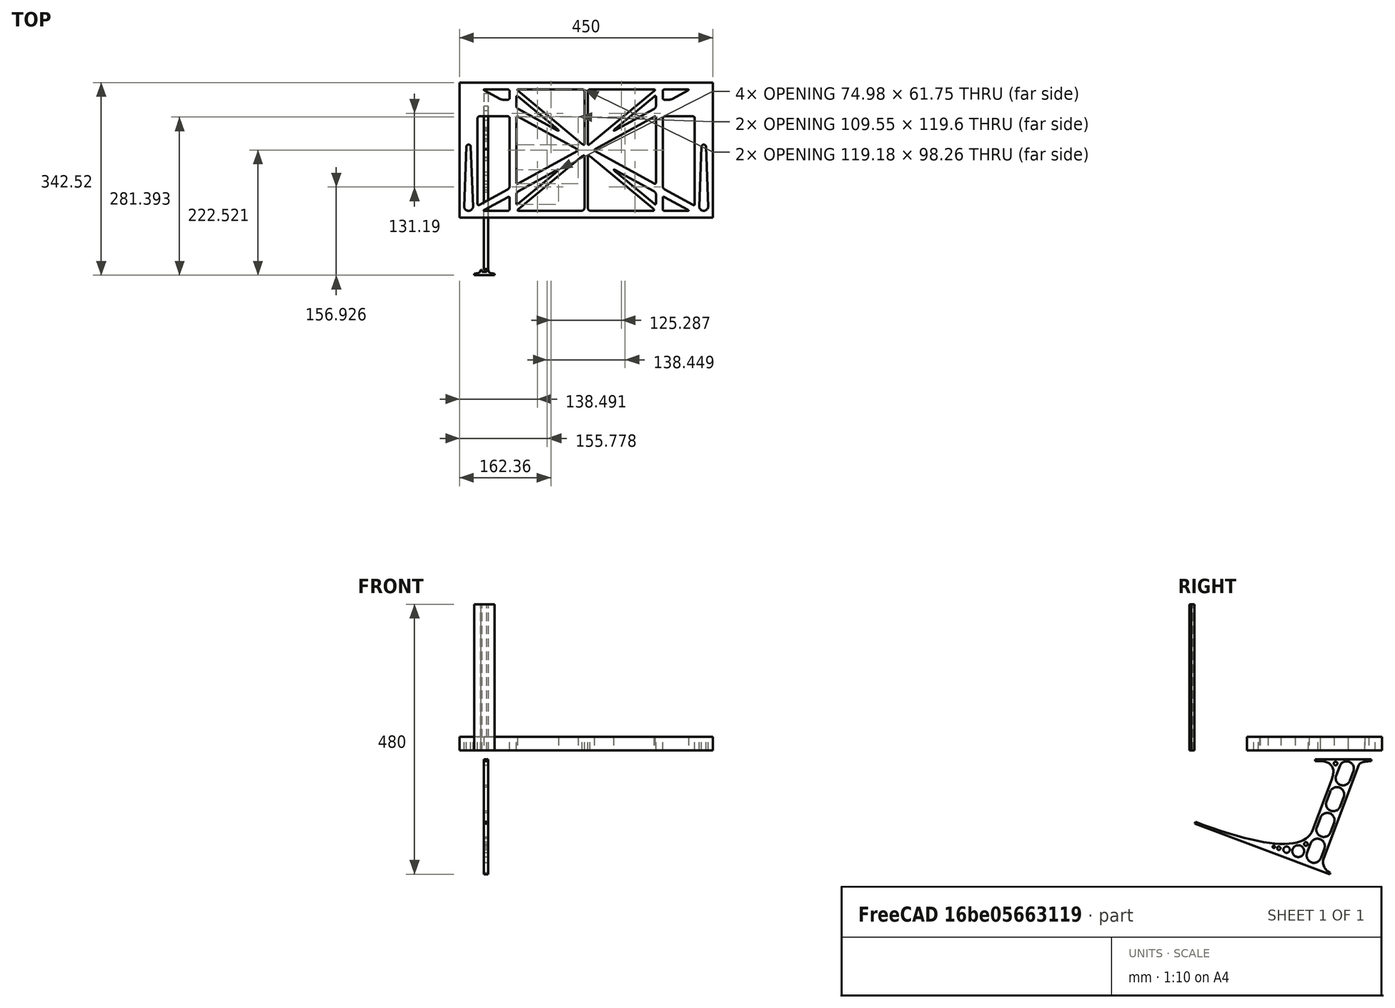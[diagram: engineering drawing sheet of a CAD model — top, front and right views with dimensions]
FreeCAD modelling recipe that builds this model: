
FCSTD DOCUMENT  (FreeCAD 0.19R0.19.2)
Label: laptopStand175FCStd
License: All rights reserved
LicenseURL: http://en.wikipedia.org/wiki/All_rights_reserved
objects: Sketcher::SketchObject×4, Part::Extrusion×3
note: 7 computed .brp shape members not serialized (recipe doc carries the construction recipe); baked Part::Feature solids carry a one-line shape summary decoded from their .brp

FEATURE [Sketcher::SketchObject] Sketch
  FullyConstrained = false
  sketch-geometry (349):
    g0: LineSegment StartX=-10.9272 StartY=-82.7794 StartZ=0 EndX=46.0728 EndY=-51.4823 EndZ=0
    g1: LineSegment StartX=-10.9272 StartY=76.4095 StartZ=0 EndX=-10.9272 EndY=-82.7794 EndZ=0
    g2: LineSegment StartX=46.0728 StartY=76.4095 StartZ=0 EndX=46.0728 EndY=-51.4823 EndZ=0
    g3: LineSegment StartX=-42.9272 StartY=136.221 StartZ=0 EndX=-42.9272 EndY=-103.779 EndZ=0
    g4: LineSegment StartX=407.073 StartY=136.221 StartZ=0 EndX=407.073 EndY=-103.779 EndZ=0
    g5: ArcOfCircle CenterX=-26.9272 CenterY=-83.7794 CenterZ=0 NormalX=0 NormalY=0 NormalZ=1 AngleXU=0 Radius=8 StartAngle=3.14159 EndAngle=6.28319
    g6: ArcOfCircle CenterX=391.073 CenterY=22.1087 CenterZ=0 NormalX=0 NormalY=0 NormalZ=1 AngleXU=0 Radius=8 StartAngle=-4.4e-15 EndAngle=3.14159
    g7: LineSegment StartX=399.073 StartY=22.1087 StartZ=0 EndX=399.073 EndY=-83.7794 EndZ=0
    g8: LineSegment StartX=383.073 StartY=22.1087 StartZ=0 EndX=383.073 EndY=-83.7794 EndZ=0
    g9: ArcOfCircle CenterX=391.073 CenterY=-83.7794 CenterZ=0 NormalX=0 NormalY=0 NormalZ=1 AngleXU=0 Radius=8 StartAngle=3.14159 EndAngle=6.28319
    g10: Circle CenterX=175.022 CenterY=27.0628 CenterZ=0 NormalX=0 NormalY=0 NormalZ=1 AngleXU=0 Radius=1
    g11: Circle CenterX=179.022 CenterY=24.8665 CenterZ=0 NormalX=0 NormalY=0 NormalZ=1 AngleXU=0 Radius=1
    g12: Circle CenterX=179.022 CenterY=27.0628 CenterZ=0 NormalX=0 NormalY=0 NormalZ=1 AngleXU=0 Radius=1
    g13: BSplineCurve PolesCount=3 KnotsCount=2 Degree=2 IsPeriodic=0
    g14: GeomPoint X=175.022 Y=27.0628 Z=0
    g15: GeomPoint X=179.022 Y=27.0628 Z=0
    g16: Circle CenterX=189.124 CenterY=27.0628 CenterZ=0 NormalX=0 NormalY=0 NormalZ=1 AngleXU=0 Radius=1
    g17: Circle CenterX=185.124 CenterY=24.8665 CenterZ=0 NormalX=0 NormalY=0 NormalZ=1 AngleXU=0 Radius=1
    g18: Circle CenterX=185.124 CenterY=27.0628 CenterZ=0 NormalX=0 NormalY=0 NormalZ=1 AngleXU=0 Radius=1
    g19: BSplineCurve PolesCount=3 KnotsCount=2 Degree=2 IsPeriodic=0
    g20: GeomPoint X=189.124 Y=27.0628 Z=0
    g21: GeomPoint X=185.124 Y=27.0628 Z=0
    g22: Circle CenterX=175.022 CenterY=5.37834 CenterZ=0 NormalX=0 NormalY=0 NormalZ=1 AngleXU=0 Radius=1
    g23: Circle CenterX=179.022 CenterY=7.57463 CenterZ=0 NormalX=0 NormalY=0 NormalZ=1 AngleXU=0 Radius=1
    g24: Circle CenterX=179.022 CenterY=5.34704 CenterZ=0 NormalX=0 NormalY=0 NormalZ=1 AngleXU=0 Radius=1
    g25: BSplineCurve PolesCount=3 KnotsCount=2 Degree=2 IsPeriodic=0
    g26: GeomPoint X=175.022 Y=5.37834 Z=0
    g27: GeomPoint X=179.022 Y=5.34704 Z=0
    g28: Circle CenterX=189.124 CenterY=5.37834 CenterZ=0 NormalX=0 NormalY=0 NormalZ=1 AngleXU=0 Radius=1
    g29: Circle CenterX=185.124 CenterY=7.57463 CenterZ=0 NormalX=0 NormalY=0 NormalZ=1 AngleXU=0 Radius=1
    g30: Circle CenterX=185.124 CenterY=5.34704 CenterZ=0 NormalX=0 NormalY=0 NormalZ=1 AngleXU=0 Radius=1
    g31: BSplineCurve PolesCount=3 KnotsCount=2 Degree=2 IsPeriodic=0
    g32: GeomPoint X=189.124 Y=5.37834 Z=0
    g33: GeomPoint X=185.124 Y=5.34704 Z=0
    g34: Circle CenterX=165.871 CenterY=18.1458 CenterZ=0 NormalX=0 NormalY=0 NormalZ=1 AngleXU=0 Radius=1
    g35: Circle CenterX=169.377 CenterY=16.2206 CenterZ=0 NormalX=0 NormalY=0 NormalZ=1 AngleXU=0 Radius=1
    g36: Circle CenterX=165.871 CenterY=14.2954 CenterZ=0 NormalX=0 NormalY=0 NormalZ=1 AngleXU=0 Radius=1
    g37: BSplineCurve PolesCount=3 KnotsCount=2 Degree=2 IsPeriodic=0
    g38: GeomPoint X=165.871 Y=18.1458 Z=0
    g39: GeomPoint X=165.871 Y=14.2954 Z=0
    g40: Circle CenterX=198.275 CenterY=18.1458 CenterZ=0 NormalX=0 NormalY=0 NormalZ=1 AngleXU=0 Radius=1
    g41: Circle CenterX=194.768 CenterY=16.2206 CenterZ=0 NormalX=0 NormalY=0 NormalZ=1 AngleXU=0 Radius=1
    g42: Circle CenterX=198.275 CenterY=14.2954 CenterZ=0 NormalX=0 NormalY=0 NormalZ=1 AngleXU=0 Radius=1
    g43: BSplineCurve PolesCount=3 KnotsCount=2 Degree=2 IsPeriodic=0
    g44: GeomPoint X=198.275 Y=18.1458 Z=0
    g45: GeomPoint X=198.275 Y=14.2954 Z=0
    g46: LineSegment StartX=407.073 StartY=-103.779 StartZ=0 EndX=-42.9272 EndY=-103.779 EndZ=0
    g47: LineSegment StartX=407.073 StartY=136.221 StartZ=0 EndX=-42.9272 EndY=136.221 EndZ=0
    g48: LineSegment StartX=46.0728 StartY=76.4095 StartZ=0 EndX=-10.9272 EndY=76.4095 EndZ=0
    g49: Circle CenterX=125.607 CenterY=54.1951 CenterZ=0 NormalX=0 NormalY=0 NormalZ=1 AngleXU=0 Radius=1
    g50: Circle CenterX=139.632 CenterY=46.4944 CenterZ=0 NormalX=0 NormalY=0 NormalZ=1 AngleXU=0 Radius=1
    g51: Circle CenterX=127.326 CenterY=56.7187 CenterZ=0 NormalX=0 NormalY=0 NormalZ=1 AngleXU=0 Radius=1
    g52: BSplineCurve PolesCount=3 KnotsCount=2 Degree=2 IsPeriodic=0
    g53: GeomPoint X=125.607 Y=54.1951 Z=0
    g54: GeomPoint X=127.326 Y=56.7187 Z=0
    g55: Circle CenterX=236.821 CenterY=56.7187 CenterZ=0 NormalX=0 NormalY=0 NormalZ=1 AngleXU=0 Radius=1
    g56: Circle CenterX=224.513 CenterY=46.4944 CenterZ=0 NormalX=0 NormalY=0 NormalZ=1 AngleXU=0 Radius=1
    g57: Circle CenterX=238.538 CenterY=54.1951 CenterZ=0 NormalX=0 NormalY=0 NormalZ=1 AngleXU=0 Radius=1
    g58: BSplineCurve PolesCount=3 KnotsCount=2 Degree=2 IsPeriodic=0
    g59: GeomPoint X=236.821 Y=56.7187 Z=0
    g60: GeomPoint X=238.538 Y=54.1951 Z=0
    g61: Circle CenterX=238.538 CenterY=-21.7539 CenterZ=0 NormalX=0 NormalY=0 NormalZ=1 AngleXU=0 Radius=1
    g62: Circle CenterX=224.513 CenterY=-14.0532 CenterZ=0 NormalX=0 NormalY=0 NormalZ=1 AngleXU=0 Radius=1
    g63: Circle CenterX=236.821 CenterY=-24.2775 CenterZ=0 NormalX=0 NormalY=0 NormalZ=1 AngleXU=0 Radius=1
    g64: BSplineCurve PolesCount=3 KnotsCount=2 Degree=2 IsPeriodic=0
    g65: GeomPoint X=238.538 Y=-21.7539 Z=0
    g66: GeomPoint X=236.821 Y=-24.2775 Z=0
    g67: Circle CenterX=125.607 CenterY=-21.7539 CenterZ=0 NormalX=0 NormalY=0 NormalZ=1 AngleXU=0 Radius=1
    g68: Circle CenterX=139.632 CenterY=-14.0532 CenterZ=0 NormalX=0 NormalY=0 NormalZ=1 AngleXU=0 Radius=1
    g69: Circle CenterX=127.325 CenterY=-24.2775 CenterZ=0 NormalX=0 NormalY=0 NormalZ=1 AngleXU=0 Radius=1
    g70: BSplineCurve PolesCount=3 KnotsCount=2 Degree=2 IsPeriodic=0
    g71: GeomPoint X=125.607 Y=-21.7539 Z=0
    g72: GeomPoint X=127.325 Y=-24.2775 Z=0
    g73: Circle CenterX=302.996 CenterY=111.695 CenterZ=0 NormalX=0 NormalY=0 NormalZ=1 AngleXU=0 Radius=1
    g74: Circle CenterX=306.073 CenterY=114.251 CenterZ=0 NormalX=0 NormalY=0 NormalZ=1 AngleXU=0 Radius=1
    g75: Circle CenterX=306.073 CenterY=110.251 CenterZ=0 NormalX=0 NormalY=0 NormalZ=1 AngleXU=0 Radius=1
    g76: BSplineCurve PolesCount=3 KnotsCount=2 Degree=2 IsPeriodic=0
    g77: GeomPoint X=302.996 Y=111.695 Z=0
    g78: GeomPoint X=306.073 Y=110.251 Z=0
    g79: Circle CenterX=306.073 CenterY=95.2763 CenterZ=0 NormalX=0 NormalY=0 NormalZ=1 AngleXU=0 Radius=1
    g80: Circle CenterX=306.073 CenterY=91.2763 CenterZ=0 NormalX=0 NormalY=0 NormalZ=1 AngleXU=0 Radius=1
    g81: Circle CenterX=302.567 CenterY=89.3511 CenterZ=0 NormalX=0 NormalY=0 NormalZ=1 AngleXU=0 Radius=1
    g82: BSplineCurve PolesCount=3 KnotsCount=2 Degree=2 IsPeriodic=0
    g83: GeomPoint X=306.073 Y=95.2763 Z=0
    g84: GeomPoint X=302.567 Y=89.3511 Z=0
    g85: LineSegment StartX=306.073 StartY=110.251 StartZ=0 EndX=306.073 EndY=95.2763 EndZ=0
    g86: LineSegment StartX=302.996 StartY=111.695 StartZ=0 EndX=236.821 EndY=56.7187 EndZ=0
    g87: LineSegment StartX=238.538 StartY=54.1951 StartZ=0 EndX=302.567 EndY=89.3511 EndZ=0
    g88: Circle CenterX=61.1496 CenterY=111.695 CenterZ=0 NormalX=0 NormalY=0 NormalZ=1 AngleXU=0 Radius=1
    g89: Circle CenterX=58.0728 CenterY=114.251 CenterZ=0 NormalX=0 NormalY=0 NormalZ=1 AngleXU=0 Radius=1
    g90: Circle CenterX=58.0728 CenterY=110.251 CenterZ=0 NormalX=0 NormalY=0 NormalZ=1 AngleXU=0 Radius=1
    g91: BSplineCurve PolesCount=3 KnotsCount=2 Degree=2 IsPeriodic=0
    g92: GeomPoint X=61.1496 Y=111.695 Z=0
    g93: GeomPoint X=58.0728 Y=110.251 Z=0
    g94: Circle CenterX=61.5791 CenterY=89.3511 CenterZ=0 NormalX=0 NormalY=0 NormalZ=1 AngleXU=0 Radius=1
    g95: Circle CenterX=58.0728 CenterY=91.2763 CenterZ=0 NormalX=0 NormalY=0 NormalZ=1 AngleXU=0 Radius=1
    g96: Circle CenterX=58.0728 CenterY=95.2763 CenterZ=0 NormalX=0 NormalY=0 NormalZ=1 AngleXU=0 Radius=1
    g97: BSplineCurve PolesCount=3 KnotsCount=2 Degree=2 IsPeriodic=0
    g98: GeomPoint X=61.5791 Y=89.3511 Z=0
    g99: GeomPoint X=58.0728 Y=95.2763 Z=0
    g100: LineSegment StartX=58.0728 StartY=110.251 StartZ=0 EndX=58.0728 EndY=95.2763 EndZ=0
    g101: LineSegment StartX=61.1496 StartY=111.695 StartZ=0 EndX=127.326 EndY=56.7187 EndZ=0
    g102: LineSegment StartX=125.607 StartY=54.1951 StartZ=0 EndX=61.5791 EndY=89.3511 EndZ=0
    g103: Circle CenterX=61.5791 CenterY=-56.9099 CenterZ=0 NormalX=0 NormalY=0 NormalZ=1 AngleXU=0 Radius=1
    g104: Circle CenterX=58.0728 CenterY=-58.8351 CenterZ=0 NormalX=0 NormalY=0 NormalZ=1 AngleXU=0 Radius=1
    g105: Circle CenterX=58.0728 CenterY=-62.8351 CenterZ=0 NormalX=0 NormalY=0 NormalZ=1 AngleXU=0 Radius=1
    g106: BSplineCurve PolesCount=3 KnotsCount=2 Degree=2 IsPeriodic=0
    g107: GeomPoint X=61.5791 Y=-56.9099 Z=0
    g108: GeomPoint X=58.0728 Y=-62.8351 Z=0
    g109: Circle CenterX=58.0728 CenterY=-77.8102 CenterZ=0 NormalX=0 NormalY=0 NormalZ=1 AngleXU=0 Radius=1
    g110: Circle CenterX=58.0728 CenterY=-81.8102 CenterZ=0 NormalX=0 NormalY=0 NormalZ=1 AngleXU=0 Radius=1
    g111: Circle CenterX=61.1496 CenterY=-79.2541 CenterZ=0 NormalX=0 NormalY=0 NormalZ=1 AngleXU=0 Radius=1
    g112: BSplineCurve PolesCount=3 KnotsCount=2 Degree=2 IsPeriodic=0
    g113: GeomPoint X=58.0728 Y=-77.8102 Z=0
    g114: GeomPoint X=61.1496 Y=-79.2541 Z=0
    g115: LineSegment StartX=58.0728 StartY=-62.8351 StartZ=0 EndX=58.0728 EndY=-77.8102 EndZ=0
    g116: LineSegment StartX=61.1496 StartY=-79.2541 StartZ=0 EndX=127.325 EndY=-24.2775 EndZ=0
    g117: LineSegment StartX=125.607 StartY=-21.7539 StartZ=0 EndX=61.5791 EndY=-56.9099 EndZ=0
    g118: Circle CenterX=302.567 CenterY=-56.9099 CenterZ=0 NormalX=0 NormalY=0 NormalZ=1 AngleXU=0 Radius=1
    g119: Circle CenterX=306.073 CenterY=-58.8351 CenterZ=0 NormalX=0 NormalY=0 NormalZ=1 AngleXU=0 Radius=1
    g120: Circle CenterX=306.073 CenterY=-62.8351 CenterZ=0 NormalX=0 NormalY=0 NormalZ=1 AngleXU=0 Radius=1
    g121: BSplineCurve PolesCount=3 KnotsCount=2 Degree=2 IsPeriodic=0
    g122: GeomPoint X=302.567 Y=-56.9099 Z=0
    g123: GeomPoint X=306.073 Y=-62.8351 Z=0
    g124: Circle CenterX=302.996 CenterY=-79.2541 CenterZ=0 NormalX=0 NormalY=0 NormalZ=1 AngleXU=0 Radius=1
    g125: Circle CenterX=306.073 CenterY=-81.8102 CenterZ=0 NormalX=0 NormalY=0 NormalZ=1 AngleXU=0 Radius=1
    g126: Circle CenterX=306.073 CenterY=-77.8102 CenterZ=0 NormalX=0 NormalY=0 NormalZ=1 AngleXU=0 Radius=1
    g127: BSplineCurve PolesCount=3 KnotsCount=2 Degree=2 IsPeriodic=0
    g128: GeomPoint X=302.996 Y=-79.2541 Z=0
    g129: GeomPoint X=306.073 Y=-77.8102 Z=0
    g130: LineSegment StartX=306.073 StartY=-62.8351 StartZ=0 EndX=306.073 EndY=-77.8102 EndZ=0
    g131: LineSegment StartX=302.996 StartY=-79.2541 StartZ=0 EndX=236.821 EndY=-24.2775 EndZ=0
    g132: LineSegment StartX=238.538 StartY=-21.7539 StartZ=0 EndX=302.567 EndY=-56.9099 EndZ=0
    g133: Circle CenterX=61.6457 CenterY=-88.8112 CenterZ=0 NormalX=0 NormalY=0 NormalZ=1 AngleXU=0 Radius=1
    g134: Circle CenterX=58.0728 CenterY=-91.7794 CenterZ=0 NormalX=0 NormalY=0 NormalZ=1 AngleXU=0 Radius=1
    g135: Circle CenterX=63.9135 CenterY=-91.7794 CenterZ=0 NormalX=0 NormalY=0 NormalZ=1 AngleXU=0 Radius=1
    g136: BSplineCurve PolesCount=3 KnotsCount=2 Degree=2 IsPeriodic=0
    g137: GeomPoint X=61.6457 Y=-88.8112 Z=0
    g138: GeomPoint X=63.9135 Y=-91.7794 Z=0
    g139: Circle CenterX=179.022 CenterY=-85.8163 CenterZ=0 NormalX=0 NormalY=0 NormalZ=1 AngleXU=0 Radius=1
    g140: Circle CenterX=179.022 CenterY=-91.7794 CenterZ=0 NormalX=0 NormalY=0 NormalZ=1 AngleXU=0 Radius=1
    g141: Circle CenterX=171.895 CenterY=-91.7794 CenterZ=0 NormalX=0 NormalY=0 NormalZ=1 AngleXU=0 Radius=1
    g142: BSplineCurve PolesCount=3 KnotsCount=2 Degree=2 IsPeriodic=0
    g143: GeomPoint X=179.022 Y=-85.8163 Z=0
    g144: GeomPoint X=171.895 Y=-91.7794 Z=0
    g145: Circle CenterX=185.124 CenterY=-86.2028 CenterZ=0 NormalX=0 NormalY=0 NormalZ=1 AngleXU=0 Radius=1
    g146: Circle CenterX=185.124 CenterY=-91.7794 CenterZ=0 NormalX=0 NormalY=0 NormalZ=1 AngleXU=0 Radius=1
    g147: Circle CenterX=191.747 CenterY=-91.7794 CenterZ=0 NormalX=0 NormalY=0 NormalZ=1 AngleXU=0 Radius=1
    g148: BSplineCurve PolesCount=3 KnotsCount=2 Degree=2 IsPeriodic=0
    g149: GeomPoint X=185.124 Y=-86.2028 Z=0
    g150: GeomPoint X=191.747 Y=-91.7794 Z=0
    g151: Circle CenterX=299.888 CenterY=-86.6413 CenterZ=0 NormalX=0 NormalY=0 NormalZ=1 AngleXU=0 Radius=1
    g152: Circle CenterX=306.073 CenterY=-91.7794 CenterZ=0 NormalX=0 NormalY=0 NormalZ=1 AngleXU=0 Radius=1
    g153: Circle CenterX=298.776 CenterY=-91.7794 CenterZ=0 NormalX=0 NormalY=0 NormalZ=1 AngleXU=0 Radius=1
    g154: BSplineCurve PolesCount=3 KnotsCount=2 Degree=2 IsPeriodic=0
    g155: GeomPoint X=299.888 Y=-86.6413 Z=0
    g156: GeomPoint X=298.776 Y=-91.7794 Z=0
    g157: LineSegment StartX=189.124 StartY=5.37834 StartZ=0 EndX=299.888 EndY=-86.6413 EndZ=0
    g158: LineSegment StartX=298.776 StartY=-91.7794 StartZ=0 EndX=191.747 EndY=-91.7794 EndZ=0
    g159: LineSegment StartX=185.124 StartY=-86.2028 StartZ=0 EndX=185.124 EndY=5.34704 EndZ=0
    g160: LineSegment StartX=179.022 StartY=5.34704 StartZ=0 EndX=179.022 EndY=-85.8163 EndZ=0
    g161: LineSegment StartX=171.895 StartY=-91.7794 StartZ=0 EndX=63.9135 EndY=-91.7794 EndZ=0
    g162: LineSegment StartX=61.6457 StartY=-88.8112 StartZ=0 EndX=175.022 EndY=5.37834 EndZ=0
    g163: Circle CenterX=302.073 CenterY=124.221 CenterZ=0 NormalX=0 NormalY=0 NormalZ=1 AngleXU=0 Radius=1
    g164: Circle CenterX=306.073 CenterY=124.221 CenterZ=0 NormalX=0 NormalY=0 NormalZ=1 AngleXU=0 Radius=1
    g165: Circle CenterX=302.996 CenterY=121.665 CenterZ=0 NormalX=0 NormalY=0 NormalZ=1 AngleXU=0 Radius=1
    g166: BSplineCurve PolesCount=3 KnotsCount=2 Degree=2 IsPeriodic=0
    g167: GeomPoint X=302.073 Y=124.221 Z=0
    g168: GeomPoint X=302.996 Y=121.665 Z=0
    g169: Circle CenterX=189.124 CenterY=124.221 CenterZ=0 NormalX=0 NormalY=0 NormalZ=1 AngleXU=0 Radius=1
    g170: Circle CenterX=185.124 CenterY=124.221 CenterZ=0 NormalX=0 NormalY=0 NormalZ=1 AngleXU=0 Radius=1
    g171: Circle CenterX=185.124 CenterY=120.221 CenterZ=0 NormalX=0 NormalY=0 NormalZ=1 AngleXU=0 Radius=1
    g172: BSplineCurve PolesCount=3 KnotsCount=2 Degree=2 IsPeriodic=0
    g173: GeomPoint X=189.124 Y=124.221 Z=0
    g174: GeomPoint X=185.124 Y=120.221 Z=0
    g175: Circle CenterX=175.022 CenterY=124.221 CenterZ=0 NormalX=0 NormalY=0 NormalZ=1 AngleXU=0 Radius=1
    g176: Circle CenterX=179.022 CenterY=124.221 CenterZ=0 NormalX=0 NormalY=0 NormalZ=1 AngleXU=0 Radius=1
    g177: Circle CenterX=179.022 CenterY=120.221 CenterZ=0 NormalX=0 NormalY=0 NormalZ=1 AngleXU=0 Radius=1
    g178: BSplineCurve PolesCount=3 KnotsCount=2 Degree=2 IsPeriodic=0
    g179: GeomPoint X=175.022 Y=124.221 Z=0
    g180: GeomPoint X=179.022 Y=120.221 Z=0
    g181: Circle CenterX=62.0728 CenterY=124.221 CenterZ=0 NormalX=0 NormalY=0 NormalZ=1 AngleXU=0 Radius=1
    g182: Circle CenterX=58.0728 CenterY=124.221 CenterZ=0 NormalX=0 NormalY=0 NormalZ=1 AngleXU=0 Radius=1
    g183: Circle CenterX=61.1496 CenterY=121.665 CenterZ=0 NormalX=0 NormalY=0 NormalZ=1 AngleXU=0 Radius=1
    g184: BSplineCurve PolesCount=3 KnotsCount=2 Degree=2 IsPeriodic=0
    g185: GeomPoint X=62.0728 Y=124.221 Z=0
    g186: GeomPoint X=61.1496 Y=121.665 Z=0
    g187: LineSegment StartX=62.0728 StartY=124.221 StartZ=0 EndX=175.022 EndY=124.221 EndZ=0
    g188: LineSegment StartX=179.022 StartY=120.221 StartZ=0 EndX=179.022 EndY=27.0628 EndZ=0
    g189: LineSegment StartX=185.124 StartY=27.0628 StartZ=0 EndX=185.124 EndY=120.221 EndZ=0
    g190: LineSegment StartX=189.124 StartY=124.221 StartZ=0 EndX=302.073 EndY=124.221 EndZ=0
    g191: LineSegment StartX=302.996 StartY=121.665 StartZ=0 EndX=189.124 EndY=27.0628 EndZ=0
    g192: LineSegment StartX=175.022 StartY=27.0628 StartZ=0 EndX=61.1496 EndY=121.665 EndZ=0
    g193: Circle CenterX=61.5791 CenterY=75.4095 CenterZ=0 NormalX=0 NormalY=0 NormalZ=1 AngleXU=0 Radius=1
    g194: Circle CenterX=58.0728 CenterY=77.3346 CenterZ=0 NormalX=0 NormalY=0 NormalZ=1 AngleXU=0 Radius=1
    g195: Circle CenterX=58.0728 CenterY=73.3346 CenterZ=0 NormalX=0 NormalY=0 NormalZ=1 AngleXU=0 Radius=1
    g196: BSplineCurve PolesCount=3 KnotsCount=2 Degree=2 IsPeriodic=0
    g197: GeomPoint X=61.5791 Y=75.4095 Z=0
    g198: GeomPoint X=58.0728 Y=73.3346 Z=0
    g199: Circle CenterX=58.0728 CenterY=-40.8935 CenterZ=0 NormalX=0 NormalY=0 NormalZ=1 AngleXU=0 Radius=1
    g200: Circle CenterX=58.0728 CenterY=-44.8935 CenterZ=0 NormalX=0 NormalY=0 NormalZ=1 AngleXU=0 Radius=1
    g201: Circle CenterX=61.5791 CenterY=-42.9683 CenterZ=0 NormalX=0 NormalY=0 NormalZ=1 AngleXU=0 Radius=1
    g202: BSplineCurve PolesCount=3 KnotsCount=2 Degree=2 IsPeriodic=0
    g203: GeomPoint X=58.0728 Y=-40.8935 Z=0
    g204: GeomPoint X=61.5791 Y=-42.9683 Z=0
    g205: LineSegment StartX=61.5791 StartY=-42.9683 StartZ=0 EndX=165.871 EndY=14.2954 EndZ=0
    g206: LineSegment StartX=165.871 StartY=18.1458 StartZ=0 EndX=61.5791 EndY=75.4095 EndZ=0
    g207: LineSegment StartX=58.0728 StartY=73.3346 StartZ=0 EndX=58.0728 EndY=-40.8935 EndZ=0
    g208: Circle CenterX=302.567 CenterY=-42.9683 CenterZ=0 NormalX=0 NormalY=0 NormalZ=1 AngleXU=0 Radius=1
    g209: Circle CenterX=306.073 CenterY=-44.8935 CenterZ=0 NormalX=0 NormalY=0 NormalZ=1 AngleXU=0 Radius=1
    g210: Circle CenterX=306.073 CenterY=-40.8935 CenterZ=0 NormalX=0 NormalY=0 NormalZ=1 AngleXU=0 Radius=1
    g211: BSplineCurve PolesCount=3 KnotsCount=2 Degree=2 IsPeriodic=0
    g212: GeomPoint X=302.567 Y=-42.9683 Z=0
    g213: GeomPoint X=306.073 Y=-40.8935 Z=0
    g214: Circle CenterX=306.073 CenterY=73.3346 CenterZ=0 NormalX=0 NormalY=0 NormalZ=1 AngleXU=0 Radius=1
    g215: Circle CenterX=306.073 CenterY=77.3346 CenterZ=0 NormalX=0 NormalY=0 NormalZ=1 AngleXU=0 Radius=1
    g216: Circle CenterX=302.567 CenterY=75.4095 CenterZ=0 NormalX=0 NormalY=0 NormalZ=1 AngleXU=0 Radius=1
    g217: BSplineCurve PolesCount=3 KnotsCount=2 Degree=2 IsPeriodic=0
    g218: GeomPoint X=306.073 Y=73.3346 Z=0
    g219: GeomPoint X=302.567 Y=75.4095 Z=0
    g220: LineSegment StartX=302.567 StartY=-42.9683 StartZ=0 EndX=198.275 EndY=14.2954 EndZ=0
    g221: LineSegment StartX=198.275 StartY=18.1458 StartZ=0 EndX=302.567 EndY=75.4095 EndZ=0
    g222: LineSegment StartX=306.073 StartY=73.3346 StartZ=0 EndX=306.073 EndY=-40.8935 EndZ=0
    g223: LineSegment StartX=322.073 StartY=105.865 StartZ=0 EndX=328.643 EndY=105.865 EndZ=0
    g224: LineSegment StartX=318.073 StartY=120.221 StartZ=0 EndX=318.073 EndY=109.865 EndZ=0
    g225: LineSegment StartX=336.157 StartY=107.779 StartZ=0 EndX=362.567 EndY=122.294 EndZ=0
    g226: Circle CenterX=362.073 CenterY=124.221 CenterZ=0 NormalX=0 NormalY=0 NormalZ=1 AngleXU=0 Radius=1
    g227: Circle CenterX=366.073 CenterY=124.221 CenterZ=0 NormalX=0 NormalY=0 NormalZ=1 AngleXU=0 Radius=1
    g228: Circle CenterX=362.567 CenterY=122.294 CenterZ=0 NormalX=0 NormalY=0 NormalZ=1 AngleXU=0 Radius=1
    g229: BSplineCurve PolesCount=3 KnotsCount=2 Degree=2 IsPeriodic=0
    g230: GeomPoint X=362.073 Y=124.221 Z=0
    g231: GeomPoint X=362.567 Y=122.294 Z=0
    g232: Circle CenterX=322.073 CenterY=124.221 CenterZ=0 NormalX=0 NormalY=0 NormalZ=1 AngleXU=0 Radius=1
    g233: Circle CenterX=318.073 CenterY=124.221 CenterZ=0 NormalX=0 NormalY=0 NormalZ=1 AngleXU=0 Radius=1
    g234: Circle CenterX=318.073 CenterY=120.221 CenterZ=0 NormalX=0 NormalY=0 NormalZ=1 AngleXU=0 Radius=1
    g235: BSplineCurve PolesCount=3 KnotsCount=2 Degree=2 IsPeriodic=0
    g236: GeomPoint X=322.073 Y=124.221 Z=0
    g237: GeomPoint X=318.073 Y=120.221 Z=0
    g238: Circle CenterX=322.073 CenterY=105.865 CenterZ=0 NormalX=0 NormalY=0 NormalZ=1 AngleXU=0 Radius=1
    g239: Circle CenterX=318.073 CenterY=105.865 CenterZ=0 NormalX=0 NormalY=0 NormalZ=1 AngleXU=0 Radius=1
    g240: Circle CenterX=318.073 CenterY=109.865 CenterZ=0 NormalX=0 NormalY=0 NormalZ=1 AngleXU=0 Radius=1
    g241: BSplineCurve PolesCount=3 KnotsCount=2 Degree=2 IsPeriodic=0
    g242: GeomPoint X=322.073 Y=105.865 Z=0
    g243: GeomPoint X=318.073 Y=109.865 Z=0
    g244: Circle CenterX=336.157 CenterY=107.779 CenterZ=0 NormalX=0 NormalY=0 NormalZ=1 AngleXU=0 Radius=1
    g245: Circle CenterX=332.651 CenterY=105.853 CenterZ=0 NormalX=0 NormalY=0 NormalZ=1 AngleXU=0 Radius=1
    g246: Circle CenterX=328.643 CenterY=105.865 CenterZ=0 NormalX=0 NormalY=0 NormalZ=1 AngleXU=0 Radius=1
    g247: BSplineCurve PolesCount=3 KnotsCount=2 Degree=2 IsPeriodic=0
    g248: GeomPoint X=336.157 Y=107.779 Z=0
    g249: GeomPoint X=328.643 Y=105.865 Z=0
    g250: LineSegment StartX=322.073 StartY=124.221 StartZ=0 EndX=362.073 EndY=124.221 EndZ=0
    g251: Circle CenterX=371.567 CenterY=-80.8644 CenterZ=0 NormalX=0 NormalY=0 NormalZ=1 AngleXU=0 Radius=1
    g252: Circle CenterX=375.073 CenterY=-82.7896 CenterZ=0 NormalX=0 NormalY=0 NormalZ=1 AngleXU=0 Radius=1
    g253: Circle CenterX=375.073 CenterY=-78.7896 CenterZ=0 NormalX=0 NormalY=0 NormalZ=1 AngleXU=0 Radius=1
    g254: BSplineCurve PolesCount=3 KnotsCount=2 Degree=2 IsPeriodic=0
    g255: GeomPoint X=371.567 Y=-80.8644 Z=0
    g256: GeomPoint X=375.073 Y=-78.7896 Z=0
    g257: Circle CenterX=321.579 CenterY=-53.4075 CenterZ=0 NormalX=0 NormalY=0 NormalZ=1 AngleXU=0 Radius=1
    g258: Circle CenterX=318.073 CenterY=-51.4823 CenterZ=0 NormalX=0 NormalY=0 NormalZ=1 AngleXU=0 Radius=1
    g259: Circle CenterX=318.073 CenterY=-47.4805 CenterZ=0 NormalX=0 NormalY=0 NormalZ=1 AngleXU=0 Radius=1
    g260: BSplineCurve PolesCount=3 KnotsCount=2 Degree=2 IsPeriodic=0
    g261: GeomPoint X=321.579 Y=-53.4075 Z=0
    g262: GeomPoint X=318.073 Y=-47.4805 Z=0
    g263: LineSegment StartX=371.567 StartY=-80.8644 StartZ=0 EndX=321.579 EndY=-53.4075 EndZ=0
    g264: Circle CenterX=321.579 CenterY=-67.3492 CenterZ=0 NormalX=0 NormalY=0 NormalZ=1 AngleXU=0 Radius=1
    g265: Circle CenterX=318.073 CenterY=-65.424 CenterZ=0 NormalX=0 NormalY=0 NormalZ=1 AngleXU=0 Radius=1
    g266: Circle CenterX=318.073 CenterY=-69.424 CenterZ=0 NormalX=0 NormalY=0 NormalZ=1 AngleXU=0 Radius=1
    g267: BSplineCurve PolesCount=3 KnotsCount=2 Degree=2 IsPeriodic=0
    g268: GeomPoint X=321.579 Y=-67.3492 Z=0
    g269: GeomPoint X=318.073 Y=-69.424 Z=0
    g270: Circle CenterX=362.567 CenterY=-89.8542 CenterZ=0 NormalX=0 NormalY=0 NormalZ=1 AngleXU=0 Radius=1
    g271: Circle CenterX=366.073 CenterY=-91.7794 CenterZ=0 NormalX=0 NormalY=0 NormalZ=1 AngleXU=0 Radius=1
    g272: Circle CenterX=362.073 CenterY=-91.7794 CenterZ=0 NormalX=0 NormalY=0 NormalZ=1 AngleXU=0 Radius=1
    g273: BSplineCurve PolesCount=3 KnotsCount=2 Degree=2 IsPeriodic=0
    g274: GeomPoint X=362.567 Y=-89.8542 Z=0
    g275: GeomPoint X=362.073 Y=-91.7794 Z=0
    g276: Circle CenterX=322.073 CenterY=-91.7794 CenterZ=0 NormalX=0 NormalY=0 NormalZ=1 AngleXU=0 Radius=1
    g277: Circle CenterX=318.073 CenterY=-91.7794 CenterZ=0 NormalX=0 NormalY=0 NormalZ=1 AngleXU=0 Radius=1
    g278: Circle CenterX=318.073 CenterY=-87.7794 CenterZ=0 NormalX=0 NormalY=0 NormalZ=1 AngleXU=0 Radius=1
    g279: BSplineCurve PolesCount=3 KnotsCount=2 Degree=2 IsPeriodic=0
    g280: GeomPoint X=322.073 Y=-91.7794 Z=0
    g281: GeomPoint X=318.073 Y=-87.7794 Z=0
    g282: LineSegment StartX=362.567 StartY=-89.8542 StartZ=0 EndX=321.579 EndY=-67.3492 EndZ=0
    g283: LineSegment StartX=318.073 StartY=-69.424 StartZ=0 EndX=318.073 EndY=-87.7794 EndZ=0
    g284: LineSegment StartX=322.073 StartY=-91.7794 StartZ=0 EndX=362.073 EndY=-91.7794 EndZ=0
    g285: Circle CenterX=2.07281 CenterY=124.221 CenterZ=0 NormalX=0 NormalY=0 NormalZ=1 AngleXU=0 Radius=1
    g286: Circle CenterX=1.57905 CenterY=122.295 CenterZ=0 NormalX=0 NormalY=0 NormalZ=1 AngleXU=0 Radius=1
    g287: BSplineCurve PolesCount=3 KnotsCount=2 Degree=2 IsPeriodic=0
    g288: GeomPoint X=2.07281 Y=124.221 Z=0
    g289: GeomPoint X=1.57905 Y=122.295 Z=0
    g290: Circle CenterX=42.0728 CenterY=124.221 CenterZ=0 NormalX=0 NormalY=0 NormalZ=1 AngleXU=0 Radius=1
    g291: Circle CenterX=46.0728 CenterY=124.221 CenterZ=0 NormalX=0 NormalY=0 NormalZ=1 AngleXU=0 Radius=1
    g292: Circle CenterX=46.0728 CenterY=120.221 CenterZ=0 NormalX=0 NormalY=0 NormalZ=1 AngleXU=0 Radius=1
    g293: BSplineCurve PolesCount=3 KnotsCount=2 Degree=2 IsPeriodic=0
    g294: GeomPoint X=42.0728 Y=124.221 Z=0
    g295: GeomPoint X=46.0728 Y=120.221 Z=0
    g296: Circle CenterX=46.0728 CenterY=109.865 CenterZ=0 NormalX=0 NormalY=0 NormalZ=1 AngleXU=0 Radius=1
    g297: Circle CenterX=46.0728 CenterY=105.865 CenterZ=0 NormalX=0 NormalY=0 NormalZ=1 AngleXU=0 Radius=1
    g298: Circle CenterX=42.0728 CenterY=105.865 CenterZ=0 NormalX=0 NormalY=0 NormalZ=1 AngleXU=0 Radius=1
    g299: BSplineCurve PolesCount=3 KnotsCount=2 Degree=2 IsPeriodic=0
    g300: GeomPoint X=46.0728 Y=109.865 Z=0
    g301: GeomPoint X=42.0728 Y=105.865 Z=0
    g302: Circle CenterX=35.5028 CenterY=105.865 CenterZ=0 NormalX=0 NormalY=0 NormalZ=1 AngleXU=0 Radius=1
    g303: Circle CenterX=31.5028 CenterY=105.865 CenterZ=0 NormalX=0 NormalY=0 NormalZ=1 AngleXU=0 Radius=1
    g304: Circle CenterX=27.9965 CenterY=107.79 CenterZ=0 NormalX=0 NormalY=0 NormalZ=1 AngleXU=0 Radius=1
    g305: BSplineCurve PolesCount=3 KnotsCount=2 Degree=2 IsPeriodic=0
    g306: GeomPoint X=35.5028 Y=105.865 Z=0
    g307: GeomPoint X=27.9965 Y=107.79 Z=0
    g308: LineSegment StartX=2.07281 StartY=124.221 StartZ=0 EndX=42.0728 EndY=124.221 EndZ=0
    g309: LineSegment StartX=46.0728 StartY=120.221 StartZ=0 EndX=46.0728 EndY=109.865 EndZ=0
    g310: LineSegment StartX=42.0728 StartY=105.865 StartZ=0 EndX=35.5028 EndY=105.865 EndZ=0
    g311: LineSegment StartX=27.9965 StartY=107.79 StartZ=0 EndX=1.57905 EndY=122.295 EndZ=0
    g312: Circle CenterX=42.5666 CenterY=-67.3492 CenterZ=0 NormalX=0 NormalY=0 NormalZ=1 AngleXU=0 Radius=1
    g313: Circle CenterX=46.0728 CenterY=-65.424 CenterZ=0 NormalX=0 NormalY=0 NormalZ=1 AngleXU=0 Radius=1
    g314: Circle CenterX=46.0728 CenterY=-69.424 CenterZ=0 NormalX=0 NormalY=0 NormalZ=1 AngleXU=0 Radius=1
    g315: BSplineCurve PolesCount=3 KnotsCount=2 Degree=2 IsPeriodic=0
    g316: GeomPoint X=42.5666 Y=-67.3492 Z=0
    g317: GeomPoint X=46.0728 Y=-69.424 Z=0
    g318: Circle CenterX=46.0728 CenterY=-87.7794 CenterZ=0 NormalX=0 NormalY=0 NormalZ=1 AngleXU=0 Radius=1
    g319: Circle CenterX=46.0728 CenterY=-91.7794 CenterZ=0 NormalX=0 NormalY=0 NormalZ=1 AngleXU=0 Radius=1
    g320: Circle CenterX=42.0728 CenterY=-91.7794 CenterZ=0 NormalX=0 NormalY=0 NormalZ=1 AngleXU=0 Radius=1
    g321: BSplineCurve PolesCount=3 KnotsCount=2 Degree=2 IsPeriodic=0
    g322: GeomPoint X=46.0728 Y=-87.7794 Z=0
    g323: GeomPoint X=42.0728 Y=-91.7794 Z=0
    g324: Circle CenterX=2.07281 CenterY=-91.7794 CenterZ=0 NormalX=0 NormalY=0 NormalZ=1 AngleXU=0 Radius=1
    g325: Circle CenterX=-1.92719 CenterY=-91.7794 CenterZ=0 NormalX=0 NormalY=0 NormalZ=1 AngleXU=0 Radius=1
    g326: Circle CenterX=1.57905 CenterY=-89.8542 CenterZ=0 NormalX=0 NormalY=0 NormalZ=1 AngleXU=0 Radius=1
    g327: BSplineCurve PolesCount=3 KnotsCount=2 Degree=2 IsPeriodic=0
    g328: GeomPoint X=2.07281 Y=-91.7794 Z=0
    g329: GeomPoint X=1.57905 Y=-89.8542 Z=0
    g330: LineSegment StartX=2.07281 StartY=-91.7794 StartZ=0 EndX=42.0728 EndY=-91.7794 EndZ=0
    g331: LineSegment StartX=46.0728 StartY=-87.7794 StartZ=0 EndX=46.0728 EndY=-69.424 EndZ=0
    g332: LineSegment StartX=42.5666 StartY=-67.3492 StartZ=0 EndX=1.57905 EndY=-89.8542 EndZ=0
    g333: Circle CenterX=322.073 CenterY=76.4095 CenterZ=0 NormalX=0 NormalY=0 NormalZ=1 AngleXU=0 Radius=4
    g334: BSplineCurve PolesCount=3 KnotsCount=2 Degree=2 IsPeriodic=0
    g335: GeomPoint X=318.073 Y=72.4095 Z=0
    g336: GeomPoint X=322.073 Y=76.4095 Z=0
    g337: Circle CenterX=375.073 CenterY=72.4095 CenterZ=0 NormalX=0 NormalY=0 NormalZ=1 AngleXU=0 Radius=1
    g338: Circle CenterX=375.073 CenterY=76.4095 CenterZ=0 NormalX=0 NormalY=0 NormalZ=1 AngleXU=0 Radius=1
    g339: Circle CenterX=371.073 CenterY=76.4095 CenterZ=0 NormalX=0 NormalY=0 NormalZ=1 AngleXU=0 Radius=1
    g340: BSplineCurve PolesCount=3 KnotsCount=2 Degree=2 IsPeriodic=0
    g341: GeomPoint X=375.073 Y=72.4095 Z=0
    g342: GeomPoint X=371.073 Y=76.4095 Z=0
    g343: LineSegment StartX=322.073 StartY=76.4095 StartZ=0 EndX=371.073 EndY=76.4095 EndZ=0
    g344: LineSegment StartX=318.073 StartY=72.4095 StartZ=0 EndX=318.073 EndY=-47.4805 EndZ=0
    g345: LineSegment StartX=375.073 StartY=72.4095 StartZ=0 EndX=375.073 EndY=-78.7896 EndZ=0
    g346: ArcOfCircle CenterX=-26.9272 CenterY=22.1087 CenterZ=0 NormalX=0 NormalY=0 NormalZ=1 AngleXU=0 Radius=4 StartAngle=5e-16 EndAngle=3.14159
    g347: LineSegment StartX=-30.9272 StartY=22.1087 StartZ=0 EndX=-34.9272 EndY=-83.7794 EndZ=0
    g348: LineSegment StartX=-18.9272 StartY=-83.7794 StartZ=0 EndX=-22.9272 EndY=22.1087 EndZ=0
  constraints (572):
    c: Coincident(g0,g2)
    c: Block(g0)
    c: Block(g1)
    c: Vertical(g3)
    c: Vertical(g4)
    c: Block(g4)
    c: Block(g3)
    c: Tangent(g6,g7) = 1.5708
    c: Tangent(g7,g9) = 1.5708
    c: Equal(g6,g9)
    c: Coincident(g8,g6)
    c: Coincident(g8,g9)
    c: Block(g7)
    c: Block(g8)
    c: Weight(g10) = 1
    c: Equal(g10,g11)
    c: Equal(g10,g12)
    c: InternalAlignment(g10,g13)
    c: InternalAlignment(g11,g13)
    c: InternalAlignment(g12,g13)
    c: InternalAlignment(g14,g13)
    c: InternalAlignment(g15,g13)
    c: Weight(g16) = 1
    c: Equal(g16,g17)
    c: Equal(g16,g18)
    c: InternalAlignment(g16,g19)
    c: InternalAlignment(g17,g19)
    c: InternalAlignment(g18,g19)
    c: InternalAlignment(g20,g19)
    c: InternalAlignment(g21,g19)
    c: Block(g19)
    c: Block(g13)
    c: Weight(g22) = 1
    c: Equal(g22,g23)
    c: Equal(g22,g24)
    c: InternalAlignment(g22,g25)
    c: InternalAlignment(g23,g25)
    c: InternalAlignment(g24,g25)
    c: InternalAlignment(g26,g25)
    c: InternalAlignment(g27,g25)
    c: Weight(g28) = 1
    c: Equal(g28,g29)
    c: Equal(g28,g30)
    c: InternalAlignment(g28,g31)
    c: InternalAlignment(g29,g31)
    c: InternalAlignment(g30,g31)
    c: InternalAlignment(g32,g31)
    c: InternalAlignment(g33,g31)
    c: Block(g31)
    c: Block(g25)
    c: Weight(g34) = 1
    c: Equal(g34,g35)
    c: Equal(g34,g36)
    c: InternalAlignment(g34,g37)
    c: InternalAlignment(g35,g37)
    c: InternalAlignment(g36,g37)
    c: InternalAlignment(g38,g37)
    c: InternalAlignment(g39,g37)
    c: Weight(g40) = 1
    c: Equal(g40,g41)
    c: Equal(g40,g42)
    c: InternalAlignment(g40,g43)
    c: InternalAlignment(g41,g43)
    c: InternalAlignment(g42,g43)
    c: InternalAlignment(g44,g43)
    c: InternalAlignment(g45,g43)
    c: Block(g37)
    c: Block(g43)
    c: Coincident(g46,g4)
    c: Coincident(g46,g3)
    c: Horizontal(g46)
    c: Distance(g46) = 450
    c: Coincident(g47,g4)
    c: Coincident(g47,g3)
    c: Horizontal(g47)
    c: Horizontal(g48)
    c: Coincident(g2,g48)
    c: Block(g48)
    c: Coincident(g1,g48)
    c: Weight(g49) = 1
    c: Equal(g49,g50)
    c: Equal(g49,g51)
    c: InternalAlignment(g49,g52)
    c: InternalAlignment(g50,g52)
    c: InternalAlignment(g51,g52)
    c: InternalAlignment(g53,g52)
    c: InternalAlignment(g54,g52)
    c: Block(g52)
    c: Weight(g55) = 1
    c: Equal(g55,g56)
    c: Equal(g55,g57)
    c: InternalAlignment(g55,g58)
    c: InternalAlignment(g56,g58)
    c: InternalAlignment(g57,g58)
    c: InternalAlignment(g59,g58)
    c: InternalAlignment(g60,g58)
    c: Block(g58)
    c: Weight(g61) = 1
    c: Equal(g61,g62)
    c: Equal(g61,g63)
    c: InternalAlignment(g61,g64)
    c: InternalAlignment(g62,g64)
    c: InternalAlignment(g63,g64)
    c: InternalAlignment(g65,g64)
    c: InternalAlignment(g66,g64)
    c: Block(g64)
    c: Weight(g67) = 1
    c: Equal(g67,g68)
    c: Equal(g67,g69)
    c: InternalAlignment(g67,g70)
    c: InternalAlignment(g68,g70)
    c: InternalAlignment(g69,g70)
    c: InternalAlignment(g71,g70)
    c: InternalAlignment(g72,g70)
    c: Block(g70)
    c: Weight(g73) = 1
    c: Equal(g73,g74)
    c: Equal(g73,g75)
    c: InternalAlignment(g73,g76)
    c: InternalAlignment(g74,g76)
    c: InternalAlignment(g75,g76)
    c: InternalAlignment(g77,g76)
    c: InternalAlignment(g78,g76)
    c: Weight(g79) = 1
    c: Equal(g79,g80)
    c: Equal(g79,g81)
    c: InternalAlignment(g79,g82)
    c: InternalAlignment(g80,g82)
    c: InternalAlignment(g81,g82)
    c: InternalAlignment(g83,g82)
    c: InternalAlignment(g84,g82)
    c: Block(g76)
    c: Block(g82)
    c: Coincident(g85,g76)
    c: Coincident(g85,g82)
    c: Vertical(g85)
    c: Coincident(g86,g76)
    c: Coincident(g86,g58)
    c: Coincident(g87,g58)
    c: Coincident(g87,g82)
    c: Weight(g88) = 1
    c: Equal(g88,g89)
    c: Equal(g88,g90)
    c: InternalAlignment(g88,g91)
    c: InternalAlignment(g89,g91)
    c: InternalAlignment(g90,g91)
    c: InternalAlignment(g92,g91)
    c: InternalAlignment(g93,g91)
    c: Weight(g94) = 1
    c: Equal(g94,g95)
    c: Equal(g94,g96)
    c: InternalAlignment(g94,g97)
    c: InternalAlignment(g95,g97)
    c: InternalAlignment(g96,g97)
    c: InternalAlignment(g98,g97)
    c: InternalAlignment(g99,g97)
    c: Block(g91)
    c: Block(g97)
    c: Coincident(g100,g91)
    c: Coincident(g100,g97)
    c: Vertical(g100)
    c: Coincident(g101,g91)
    c: Coincident(g101,g52)
    c: Coincident(g102,g52)
    c: Coincident(g102,g97)
    c: Weight(g103) = 1
    c: Equal(g103,g104)
    c: Equal(g103,g105)
    c: InternalAlignment(g103,g106)
    c: InternalAlignment(g104,g106)
    c: InternalAlignment(g105,g106)
    c: InternalAlignment(g107,g106)
    c: InternalAlignment(g108,g106)
    c: Weight(g109) = 1
    c: Equal(g109,g110)
    c: Equal(g109,g111)
    c: InternalAlignment(g109,g112)
    c: InternalAlignment(g110,g112)
    c: InternalAlignment(g111,g112)
    c: InternalAlignment(g113,g112)
    c: InternalAlignment(g114,g112)
    c: Block(g106)
    c: Block(g112)
    c: Coincident(g115,g106)
    c: Coincident(g115,g112)
    c: Vertical(g115)
    c: Coincident(g116,g112)
    c: Coincident(g116,g70)
    c: Coincident(g117,g70)
    c: Coincident(g117,g106)
    c: Weight(g118) = 1
    c: Equal(g118,g119)
    c: Equal(g118,g120)
    c: InternalAlignment(g118,g121)
    c: InternalAlignment(g119,g121)
    c: InternalAlignment(g120,g121)
    c: InternalAlignment(g122,g121)
    c: InternalAlignment(g123,g121)
    c: Weight(g124) = 1
    c: Equal(g124,g125)
    c: Equal(g124,g126)
    c: InternalAlignment(g124,g127)
    c: InternalAlignment(g125,g127)
    c: InternalAlignment(g126,g127)
    c: InternalAlignment(g128,g127)
    c: InternalAlignment(g129,g127)
    c: Block(g121)
    c: Block(g127)
    c: Coincident(g130,g121)
    c: Coincident(g130,g127)
    c: Vertical(g130)
    c: Coincident(g131,g127)
    c: Coincident(g131,g64)
    c: Coincident(g132,g64)
    c: Coincident(g132,g121)
    c: Weight(g133) = 1
    c: Equal(g133,g134)
    c: Equal(g133,g135)
    c: InternalAlignment(g133,g136)
    c: InternalAlignment(g134,g136)
    c: InternalAlignment(g135,g136)
    c: InternalAlignment(g137,g136)
    c: InternalAlignment(g138,g136)
    c: Weight(g139) = 1
    c: Equal(g139,g140)
    c: Equal(g139,g141)
    c: InternalAlignment(g139,g142)
    c: InternalAlignment(g140,g142)
    c: InternalAlignment(g141,g142)
    c: InternalAlignment(g143,g142)
    c: InternalAlignment(g144,g142)
    c: Weight(g145) = 1
    c: Equal(g145,g146)
    c: Equal(g145,g147)
    c: InternalAlignment(g145,g148)
    c: InternalAlignment(g146,g148)
    c: InternalAlignment(g147,g148)
    c: InternalAlignment(g149,g148)
    c: InternalAlignment(g150,g148)
    c: Weight(g151) = 1
    c: Equal(g151,g152)
    c: Equal(g151,g153)
    c: InternalAlignment(g151,g154)
    c: InternalAlignment(g152,g154)
    c: InternalAlignment(g153,g154)
    c: InternalAlignment(g155,g154)
    c: InternalAlignment(g156,g154)
    c: Block(g154)
    c: Block(g148)
    c: Block(g142)
    c: Block(g136)
    c: Coincident(g157,g31)
    c: Coincident(g157,g154)
    c: Coincident(g158,g154)
    c: Coincident(g158,g148)
    c: Horizontal(g158)
    c: Coincident(g159,g148)
    c: Coincident(g159,g31)
    c: Vertical(g159)
    c: Coincident(g160,g25)
    c: Coincident(g160,g142)
    c: Vertical(g160)
    c: Coincident(g161,g142)
    c: Coincident(g161,g136)
    c: Horizontal(g161)
    c: Coincident(g162,g136)
    c: Coincident(g162,g25)
    c: Weight(g163) = 1
    c: Equal(g163,g164)
    c: Equal(g163,g165)
    c: InternalAlignment(g163,g166)
    c: InternalAlignment(g164,g166)
    c: InternalAlignment(g165,g166)
    c: InternalAlignment(g167,g166)
    c: InternalAlignment(g168,g166)
    c: Weight(g169) = 1
    c: Equal(g169,g170)
    c: Equal(g169,g171)
    c: InternalAlignment(g169,g172)
    c: InternalAlignment(g170,g172)
    c: InternalAlignment(g171,g172)
    c: InternalAlignment(g173,g172)
    c: InternalAlignment(g174,g172)
    c: Weight(g175) = 1
    c: Equal(g175,g176)
    c: Equal(g175,g177)
    c: InternalAlignment(g175,g178)
    c: InternalAlignment(g176,g178)
    c: InternalAlignment(g177,g178)
    c: InternalAlignment(g179,g178)
    c: InternalAlignment(g180,g178)
    c: Weight(g181) = 1
    c: Equal(g181,g182)
    c: Equal(g181,g183)
    c: InternalAlignment(g181,g184)
    c: InternalAlignment(g182,g184)
    c: InternalAlignment(g183,g184)
    c: InternalAlignment(g185,g184)
    c: InternalAlignment(g186,g184)
    c: Block(g184)
    c: Block(g178)
    c: Block(g172)
    c: Block(g166)
    c: Coincident(g187,g184)
    c: Coincident(g187,g178)
    c: Horizontal(g187)
    c: Coincident(g188,g178)
    c: Coincident(g188,g13)
    c: Vertical(g188)
    c: Coincident(g189,g19)
    c: Coincident(g189,g172)
    c: Vertical(g189)
    c: Coincident(g190,g172)
    c: Coincident(g190,g166)
    c: Horizontal(g190)
    c: Coincident(g191,g166)
    c: Coincident(g191,g19)
    c: Coincident(g192,g13)
    c: Weight(g193) = 1
    c: Equal(g193,g194)
    c: Equal(g193,g195)
    c: InternalAlignment(g193,g196)
    c: InternalAlignment(g194,g196)
    c: InternalAlignment(g195,g196)
    c: InternalAlignment(g197,g196)
    c: InternalAlignment(g198,g196)
    c: Weight(g199) = 1
    c: Equal(g199,g200)
    c: Equal(g199,g201)
    c: InternalAlignment(g199,g202)
    c: InternalAlignment(g200,g202)
    c: InternalAlignment(g201,g202)
    c: InternalAlignment(g203,g202)
    c: InternalAlignment(g204,g202)
    c: Block(g202)
    c: Block(g196)
    c: Coincident(g205,g202)
    c: Coincident(g205,g37)
    c: Coincident(g206,g37)
    c: Coincident(g206,g196)
    c: Coincident(g207,g196)
    c: Coincident(g207,g202)
    c: Vertical(g207)
    c: Weight(g208) = 1
    c: Equal(g208,g209)
    c: Equal(g208,g210)
    c: InternalAlignment(g208,g211)
    c: InternalAlignment(g209,g211)
    c: InternalAlignment(g210,g211)
    c: InternalAlignment(g212,g211)
    c: InternalAlignment(g213,g211)
    c: Weight(g214) = 1
    c: Equal(g214,g215)
    c: Equal(g214,g216)
    c: InternalAlignment(g214,g217)
    c: InternalAlignment(g215,g217)
    c: InternalAlignment(g216,g217)
    c: InternalAlignment(g218,g217)
    c: InternalAlignment(g219,g217)
    c: Block(g217)
    c: Block(g211)
    c: Coincident(g220,g211)
    c: Coincident(g220,g43)
    c: Coincident(g221,g43)
    c: Coincident(g221,g217)
    c: Coincident(g222,g217)
    c: Coincident(g222,g211)
    c: Vertical(g222)
    c: Horizontal(g223)
    c: Block(g223)
    c: Vertical(g224)
    c: Block(g224)
    c: Block(g225)
    c: Weight(g226) = 1
    c: Equal(g226,g227)
    c: Equal(g226,g228)
    c: InternalAlignment(g226,g229)
    c: InternalAlignment(g227,g229)
    c: InternalAlignment(g228,g229)
    c: InternalAlignment(g230,g229)
    c: InternalAlignment(g231,g229)
    c: Weight(g232) = 1
    c: Equal(g232,g233)
    c: Equal(g232,g234)
    c: InternalAlignment(g232,g235)
    c: InternalAlignment(g233,g235)
    c: InternalAlignment(g234,g235)
    c: InternalAlignment(g236,g235)
    c: InternalAlignment(g237,g235)
    c: Weight(g238) = 1
    c: Equal(g238,g239)
    c: Equal(g238,g240)
    c: InternalAlignment(g238,g241)
    c: InternalAlignment(g239,g241)
    c: InternalAlignment(g240,g241)
    c: InternalAlignment(g242,g241)
    c: InternalAlignment(g243,g241)
    c: Weight(g244) = 1
    c: Equal(g244,g245)
    c: Equal(g244,g246)
    c: InternalAlignment(g244,g247)
    c: InternalAlignment(g245,g247)
    c: InternalAlignment(g246,g247)
    c: InternalAlignment(g248,g247)
    c: InternalAlignment(g249,g247)
    c: Block(g229)
    c: Block(g235)
    c: Block(g241)
    c: Block(g247)
    c: Coincident(g250,g235)
    c: Coincident(g250,g229)
    c: Horizontal(g250)
    c: Block(g192)
    c: Weight(g251) = 1
    c: Equal(g251,g252)
    c: Equal(g251,g253)
    c: InternalAlignment(g251,g254)
    c: InternalAlignment(g252,g254)
    c: InternalAlignment(g253,g254)
    c: InternalAlignment(g255,g254)
    c: InternalAlignment(g256,g254)
    c: Weight(g257) = 1
    c: Equal(g257,g258)
    c: Equal(g257,g259)
    c: InternalAlignment(g257,g260)
    c: InternalAlignment(g258,g260)
    c: InternalAlignment(g259,g260)
    c: InternalAlignment(g261,g260)
    c: InternalAlignment(g262,g260)
    c: Block(g254)
    c: Block(g260)
    c: Coincident(g263,g254)
    c: Coincident(g263,g260)
    c: Weight(g264) = 1
    c: Equal(g264,g265)
    c: Equal(g264,g266)
    c: InternalAlignment(g264,g267)
    c: InternalAlignment(g265,g267)
    c: InternalAlignment(g266,g267)
    c: InternalAlignment(g268,g267)
    c: InternalAlignment(g269,g267)
    c: Weight(g270) = 1
    c: Equal(g270,g271)
    c: Equal(g270,g272)
    c: InternalAlignment(g270,g273)
    c: InternalAlignment(g271,g273)
    c: InternalAlignment(g272,g273)
    c: InternalAlignment(g274,g273)
    c: InternalAlignment(g275,g273)
    c: Weight(g276) = 1
    c: Equal(g276,g277)
    c: Equal(g276,g278)
    c: InternalAlignment(g276,g279)
    c: InternalAlignment(g277,g279)
    c: InternalAlignment(g278,g279)
    c: InternalAlignment(g280,g279)
    c: InternalAlignment(g281,g279)
    c: Block(g279)
    c: Block(g273)
    c: Block(g267)
    c: Coincident(g282,g273)
    c: Coincident(g282,g267)
    c: Coincident(g283,g267)
    c: Coincident(g283,g279)
    c: Vertical(g283)
    c: Coincident(g284,g279)
    c: Coincident(g284,g273)
    c: Horizontal(g284)
    c: Weight(g285) = 1
    c: Equal(g285,g286)
    c: InternalAlignment(g285,g287)
    c: InternalAlignment(g286,g287)
    c: InternalAlignment(g288,g287)
    c: InternalAlignment(g289,g287)
    c: Weight(g290) = 1
    c: InternalAlignment(g291,g293)
    c: InternalAlignment(g292,g293)
    c: InternalAlignment(g294,g293)
    c: InternalAlignment(g295,g293)
    c: Weight(g296) = 1
    c: Equal(g296,g297)
    c: Equal(g296,g298)
    c: InternalAlignment(g296,g299)
    c: InternalAlignment(g297,g299)
    c: InternalAlignment(g298,g299)
    c: InternalAlignment(g300,g299)
    c: InternalAlignment(g301,g299)
    c: Equal(g302,g303)
    c: Equal(g302,g304)
    c: InternalAlignment(g302,g305)
    c: InternalAlignment(g303,g305)
    c: InternalAlignment(g304,g305)
    c: InternalAlignment(g306,g305)
    c: InternalAlignment(g307,g305)
    c: Block(g293)
    c: Block(g299)
    c: Block(g305)
    c: Block(g287)
    c: Coincident(g308,g287)
    c: Coincident(g308,g293)
    c: Horizontal(g308)
    c: Coincident(g309,g293)
    c: Coincident(g309,g299)
    c: Vertical(g309)
    c: Coincident(g310,g299)
    c: Coincident(g310,g305)
    c: Horizontal(g310)
    c: Coincident(g311,g305)
    c: Coincident(g311,g287)
    c: Weight(g312) = 1
    c: Equal(g312,g313)
    c: Equal(g312,g314)
    c: InternalAlignment(g312,g315)
    c: InternalAlignment(g313,g315)
    c: InternalAlignment(g314,g315)
    c: InternalAlignment(g316,g315)
    c: InternalAlignment(g317,g315)
    c: Weight(g318) = 1
    c: Equal(g318,g319)
    c: Equal(g318,g320)
    c: InternalAlignment(g318,g321)
    c: InternalAlignment(g319,g321)
    c: InternalAlignment(g320,g321)
    c: InternalAlignment(g322,g321)
    c: InternalAlignment(g323,g321)
    c: Weight(g324) = 1
    c: Equal(g324,g325)
    c: Equal(g324,g326)
    c: InternalAlignment(g324,g327)
    c: InternalAlignment(g325,g327)
    c: InternalAlignment(g326,g327)
    c: InternalAlignment(g328,g327)
    c: InternalAlignment(g329,g327)
    c: Block(g327)
    c: Block(g321)
    c: Block(g315)
    c: Coincident(g330,g327)
    c: Coincident(g330,g321)
    c: Horizontal(g330)
    c: Coincident(g331,g321)
    c: Coincident(g331,g315)
    c: Vertical(g331)
    c: Coincident(g332,g315)
    c: Coincident(g332,g327)
    c: InternalAlignment(g333,g334)
    c: InternalAlignment(g335,g334)
    c: InternalAlignment(g336,g334)
    c: Block(g334)
    c: Equal(g337,g338)
    c: Equal(g337,g339)
    c: InternalAlignment(g337,g340)
    c: InternalAlignment(g338,g340)
    c: InternalAlignment(g339,g340)
    c: InternalAlignment(g341,g340)
    c: InternalAlignment(g342,g340)
    c: Block(g340)
    c: Coincident(g343,g334)
    c: Horizontal(g343)
    c: Block(g343)
    c: Coincident(g344,g334)
    c: Coincident(g344,g260)
    c: Vertical(g344)
    c: Coincident(g345,g340)
    c: Coincident(g345,g254)
    c: Vertical(g345)
    c: Coincident(g347,g5)
    c: Coincident(g348,g5)
    c: Block(g346)
    c: Block(g5)
    c: Block(g348)
    c: Block(g347)
    c: Distance(g344) = 119.89
FEATURE [Sketcher::SketchObject] Sketch001
  FullyConstrained = true
  MapMode = 4
  Placement = pos=(0,0,0) rot=(0.57735,0.57735,0.57735;2.0944rad)
  Support = -> [Sketch]
  sketch-geometry (46):
    g0: BSplineCurve PolesCount=3 KnotsCount=2 Degree=2 IsPeriodic=0
    g1: ArcOfCircle CenterX=73.1223 CenterY=-32.291 CenterZ=0 NormalX=0 NormalY=0 NormalZ=1 AngleXU=0 Radius=13 StartAngle=5.92268 EndAngle=9.06428
    g2: ArcOfCircle CenterX=66.7816 CenterY=-49.1439 CenterZ=0 NormalX=0 NormalY=0 NormalZ=1 AngleXU=0 Radius=13 StartAngle=2.78068 EndAngle=5.92131
    g3: ArcOfCircle CenterX=55.9263 CenterY=-78.1807 CenterZ=0 NormalX=0 NormalY=0 NormalZ=1 AngleXU=0 Radius=13 StartAngle=5.92268 EndAngle=9.06428
    g4: ArcOfCircle CenterX=49.5884 CenterY=-95.0342 CenterZ=0 NormalX=0 NormalY=0 NormalZ=1 AngleXU=0 Radius=13 StartAngle=2.78068 EndAngle=5.92131
    g5: ArcOfCircle CenterX=38.7206 CenterY=-124.067 CenterZ=0 NormalX=0 NormalY=0 NormalZ=1 AngleXU=0 Radius=13 StartAngle=5.92268 EndAngle=9.06428
    g6: ArcOfCircle CenterX=32.3875 CenterY=-140.92 CenterZ=0 NormalX=0 NormalY=0 NormalZ=1 AngleXU=0 Radius=13 StartAngle=2.78068 EndAngle=5.92131
    g7: ArcOfCircle CenterX=21.4715 CenterY=-169.934 CenterZ=0 NormalX=0 NormalY=0 NormalZ=1 AngleXU=0 Radius=13 StartAngle=5.92268 EndAngle=9.06428
    g8: ArcOfCircle CenterX=15.1336 CenterY=-186.787 CenterZ=0 NormalX=0 NormalY=0 NormalZ=1 AngleXU=0 Radius=13 StartAngle=2.78068 EndAngle=5.92131
    g9-g12: Circle x4 (B-spline internal-alignment scaffolding for g13; pole/knot coordinates omitted)
    g13: BSplineCurve PolesCount=4 KnotsCount=2 Degree=3 IsPeriodic=0
    g14: GeomPoint X=28.8094 Y=-19.0875 Z=0
    g15: GeomPoint X=47.0443 Y=-50.4712 Z=0
    g16: Circle CenterX=53.5586 CenterY=-23.2695 CenterZ=0 NormalX=0 NormalY=0 NormalZ=1 AngleXU=0 Radius=3.24518
    g17: Circle CenterX=-195.441 CenterY=-127.082 CenterZ=0 NormalX=0 NormalY=0 NormalZ=1 AngleXU=0 Radius=1
    g18: Circle CenterX=-8.24091 CenterY=-197.481 CenterZ=0 NormalX=0 NormalY=0 NormalZ=1 AngleXU=0 Radius=1
    g19: Circle CenterX=12.8789 CenterY=-141.321 CenterZ=0 NormalX=0 NormalY=0 NormalZ=1 AngleXU=0 Radius=1
    g20: BSplineCurve PolesCount=3 KnotsCount=2 Degree=2 IsPeriodic=0
    g21: GeomPoint X=-195.441 Y=-127.082 Z=0
    g22: GeomPoint X=12.8789 Y=-141.321 Z=0
    g23: Circle CenterX=-12.8016 CenterY=-179.036 CenterZ=0 NormalX=0 NormalY=0 NormalZ=1 AngleXU=0 Radius=10.5072
    g24: Circle CenterX=0.933922 CenterY=-166.43 CenterZ=0 NormalX=0 NormalY=0 NormalZ=1 AngleXU=0 Radius=3.26661
    g25: Circle CenterX=-33.5518 CenterY=-176.44 CenterZ=0 NormalX=0 NormalY=0 NormalZ=1 AngleXU=0 Radius=5.64388
    g26: Circle CenterX=-47.2366 CenterY=-173.859 CenterZ=0 NormalX=0 NormalY=0 NormalZ=1 AngleXU=0 Radius=3.01653
    g27: Circle CenterX=-56.2595 CenterY=-171.456 CenterZ=0 NormalX=0 NormalY=0 NormalZ=1 AngleXU=0 Radius=2.12826
    g28: ArcOfCircle CenterX=51.2151 CenterY=-198.473 CenterZ=0 NormalX=0 NormalY=0 NormalZ=1 AngleXU=0 Radius=20 StartAngle=2.78189 EndAngle=4.35269
    g29: LineSegment StartX=32.4951 StartY=-191.433 StartZ=0 EndX=94.6578 EndY=-26.1352 EndZ=0
    g30: LineSegment StartX=43.1192 StartY=-220.001 StartZ=0 EndX=-196.497 EndY=-129.89 EndZ=0
    g31: LineSegment StartX=43.1192 StartY=-220.001 StartZ=0 EndX=44.1752 EndY=-217.193 EndZ=0
    g32: LineSegment StartX=117.223 StartY=-19.0875 StartZ=0 EndX=117.223 EndY=-16.0875 EndZ=0
    g33: LineSegment StartX=117.223 StartY=-16.0875 StartZ=0 EndX=17.2232 EndY=-16.0875 EndZ=0
    g34: LineSegment StartX=17.2232 StartY=-16.0875 StartZ=0 EndX=17.2232 EndY=-19.0875 EndZ=0
    g35: LineSegment StartX=28.8094 StartY=-19.0875 StartZ=0 EndX=17.2232 EndY=-19.0875 EndZ=0
    g36: LineSegment StartX=47.0443 StartY=-50.4712 StartZ=0 EndX=12.8789 EndY=-141.321 EndZ=0
    g37: LineSegment StartX=-195.441 StartY=-127.082 StartZ=0 EndX=-196.497 EndY=-129.89 EndZ=0
    g38: LineSegment StartX=85.2866 StartY=-36.8766 StartZ=0 EndX=78.9396 EndY=-53.7463 EndZ=0
    g39: LineSegment StartX=60.9579 StartY=-27.7053 StartZ=0 EndX=54.6191 EndY=-44.5532 EndZ=0
    g40: LineSegment StartX=68.0907 StartY=-82.7664 StartZ=0 EndX=61.7465 EndY=-99.6365 EndZ=0
    g41: LineSegment StartX=43.7619 StartY=-73.595 StartZ=0 EndX=37.426 EndY=-90.4435 EndZ=0
    g42: LineSegment StartX=50.885 StartY=-128.652 StartZ=0 EndX=44.5456 EndY=-145.522 EndZ=0
    g43: LineSegment StartX=26.5562 StartY=-119.481 StartZ=0 EndX=20.2251 EndY=-136.329 EndZ=0
    g44: LineSegment StartX=9.3071 StartY=-165.349 StartZ=0 EndX=2.97115 EndY=-182.197 EndZ=0
    g45: LineSegment StartX=33.6358 StartY=-174.52 StartZ=0 EndX=27.2917 EndY=-191.39 EndZ=0
  constraints (71):
    c: Block(g0)
    c: Block(g1)
    c: Block(g2)
    c: Block(g4)
    c: Block(g3)
    c: Block(g6)
    c: Block(g5)
    c: Block(g8)
    c: Block(g7)
    c: Weight(g9) = 1
    c: Equal(g9,g10)
    c: Equal(g9,g11)
    c: Equal(g9,g12)
    c: InternalAlignment(g9-g12 -> g13) x4
    c: InternalAlignment(g14,g13)
    c: InternalAlignment(g15,g13)
    c: Block(g16)
    c: Weight(g17) = 1
    c: Equal(g17,g18)
    c: Equal(g17,g19)
    c: InternalAlignment(g17,g20)
    c: InternalAlignment(g18,g20)
    c: InternalAlignment(g19,g20)
    c: InternalAlignment(g21,g20)
    c: InternalAlignment(g22,g20)
    c: Block(g20)
    c: Block(g23)
    c: Block(g24)
    c: Block(g25)
    c: Block(g26)
    c: Block(g27)
    c: Block(g28)
    c: Coincident(g29,g28)
    c: Coincident(g29,g0)
    c: Block(g13)
    c: Coincident(g31,g30)
    c: Coincident(g31,g28)
    c: Block(g31)
    c: Coincident(g32,g0)
    c: Vertical(g32)
    c: Coincident(g33,g32)
    c: Horizontal(g33)
    c: Coincident(g34,g33)
    c: Vertical(g34)
    c: Block(g33)
    c: Coincident(g35,g13)
    c: Coincident(g35,g34)
    c: Horizontal(g35)
    c: Coincident(g36,g13)
    c: Coincident(g36,g20)
    c: Coincident(g37,g20)
    c: Coincident(g37,g30)
    c: Block(g30)
    c: Coincident(g38,g1)
    c: Coincident(g38,g2)
    c: Coincident(g39,g1)
    c: Coincident(g39,g2)
    c: Coincident(g40,g3)
    c: Coincident(g40,g4)
    c: Coincident(g41,g3)
    c: Coincident(g41,g4)
    c: Coincident(g42,g5)
    c: Coincident(g42,g6)
    c: Coincident(g43,g5)
    c: Coincident(g43,g6)
    c: Coincident(g44,g7)
    c: Coincident(g44,g8)
    c: Coincident(g45,g7)
    c: Coincident(g45,g8)
    c: Distance(g30) = 256
    c: Distance(g33) = 100
FEATURE [Part::Extrusion] Extrude002
  Base = -> Sketch001
  Dir = (1,0,0)
  DirMode = 2
  FaceMakerClass = Part::FaceMakerBullseye
  LengthFwd = 8
  LengthRev = 0
  Solid = true
  Symmetric = false
FEATURE [Sketcher::SketchObject] Sketch002
  FullyConstrained = true
  sketch-geometry (20):
    g0: LineSegment StartX=-2.77179 StartY=-200.304 StartZ=0 EndX=5.22821 EndY=-200.304 EndZ=0
    g1: LineSegment StartX=5.22821 StartY=-200.304 StartZ=0 EndX=5.22821 EndY=-197.304 EndZ=0
    g2: LineSegment StartX=-2.77179 StartY=-200.304 StartZ=0 EndX=-2.77179 EndY=-197.304 EndZ=0
    g3: LineSegment StartX=5.22821 StartY=-197.304 StartZ=0 EndX=8.22821 EndY=-197.304 EndZ=0
    g4: LineSegment StartX=-2.77179 StartY=-197.304 StartZ=0 EndX=-5.77179 EndY=-197.304 EndZ=0
    g5: LineSegment StartX=19.2282 StartY=-203.304 StartZ=0 EndX=19.2282 EndY=-206.304 EndZ=0
    g6: LineSegment StartX=-16.7718 StartY=-203.304 StartZ=0 EndX=-16.7718 EndY=-206.304 EndZ=0
    g7: LineSegment StartX=-16.7718 StartY=-206.304 StartZ=0 EndX=19.2282 EndY=-206.304 EndZ=0
    g8: Circle CenterX=-16.7718 CenterY=-203.304 CenterZ=0 NormalX=0 NormalY=0 NormalZ=1 AngleXU=0 Radius=1
    g9: Circle CenterX=-5.77179 CenterY=-203.304 CenterZ=0 NormalX=0 NormalY=0 NormalZ=1 AngleXU=0 Radius=1
    g10: Circle CenterX=-5.77179 CenterY=-197.304 CenterZ=0 NormalX=0 NormalY=0 NormalZ=1 AngleXU=0 Radius=1
    g11: BSplineCurve PolesCount=3 KnotsCount=2 Degree=2 IsPeriodic=0
    g12: GeomPoint X=-16.7718 Y=-203.304 Z=0
    g13: GeomPoint X=-5.77179 Y=-197.304 Z=0
    g14: Circle CenterX=19.2282 CenterY=-203.304 CenterZ=0 NormalX=0 NormalY=0 NormalZ=1 AngleXU=0 Radius=1
    g15: Circle CenterX=8.22821 CenterY=-203.304 CenterZ=0 NormalX=0 NormalY=0 NormalZ=1 AngleXU=0 Radius=1
    g16: Circle CenterX=8.22821 CenterY=-197.304 CenterZ=0 NormalX=0 NormalY=0 NormalZ=1 AngleXU=0 Radius=1
    g17: BSplineCurve PolesCount=3 KnotsCount=2 Degree=2 IsPeriodic=0
    g18: GeomPoint X=19.2282 Y=-203.304 Z=0
    g19: GeomPoint X=8.22821 Y=-197.304 Z=0
  constraints (41):
    c: Horizontal(g0)
    c: Distance(g0) = 8
    c: Coincident(g1,g0)
    c: Vertical(g1)
    c: Distance(g1) = 3
    c: Coincident(g2,g0)
    c: Vertical(g2)
    c: Distance(g2) = 3
    c: Coincident(g3,g1)
    c: Horizontal(g3)
    c: Distance(g3) = 3
    c: Coincident(g4,g2)
    c: Horizontal(g4)
    c: Distance(g4) = 3
    c: Vertical(g5)
    c: Vertical(g6)
    c: Coincident(g7,g6)
    c: Coincident(g7,g5)
    c: Weight(g8) = 1
    c: Equal(g8,g9)
    c: Equal(g8,g10)
    c: Coincident(g11,g4)
    c: InternalAlignment(g8,g11)
    c: InternalAlignment(g9,g11)
    c: InternalAlignment(g10,g11)
    c: InternalAlignment(g12,g11)
    c: InternalAlignment(g13,g11)
    c: Coincident(g17,g5)
    c: Weight(g14) = 1
    c: Equal(g14,g15)
    c: Equal(g14,g16)
    c: Coincident(g17,g3)
    c: InternalAlignment(g14,g17)
    c: InternalAlignment(g15,g17)
    c: InternalAlignment(g16,g17)
    c: InternalAlignment(g18,g17)
    c: InternalAlignment(g19,g17)
    c: Block(g7)
    c: Block(g17)
    c: Block(g11)
    c: Block(g6)
FEATURE [Part::Extrusion] Extrude003
  Base = -> Sketch002
  Dir = (0,0,1)
  DirMode = 2
  FaceMakerClass = Part::FaceMakerBullseye
  LengthFwd = 260
  LengthRev = 0
  Solid = true
  Symmetric = false
FEATURE [Sketcher::SketchObject] Sketch003
  FullyConstrained = false
  sketch-geometry (423):
    g0: LineSegment StartX=-42.9272 StartY=136.221 StartZ=0 EndX=-42.9272 EndY=-103.779 EndZ=0
    g1: LineSegment StartX=407.073 StartY=136.221 StartZ=0 EndX=407.073 EndY=-103.779 EndZ=0
    g2: ArcOfCircle CenterX=-26.9272 CenterY=-83.7794 CenterZ=0 NormalX=0 NormalY=0 NormalZ=1 AngleXU=0 Radius=8 StartAngle=3.14159 EndAngle=6.28319
    g3: ArcOfCircle CenterX=391.073 CenterY=-83.7794 CenterZ=0 NormalX=0 NormalY=0 NormalZ=1 AngleXU=0 Radius=8 StartAngle=3.14159 EndAngle=6.28319
    g4: Circle CenterX=175.022 CenterY=27.0628 CenterZ=0 NormalX=0 NormalY=0 NormalZ=1 AngleXU=0 Radius=1
    g5: Circle CenterX=179.022 CenterY=24.8665 CenterZ=0 NormalX=0 NormalY=0 NormalZ=1 AngleXU=0 Radius=1
    g6: Circle CenterX=179.022 CenterY=27.0628 CenterZ=0 NormalX=0 NormalY=0 NormalZ=1 AngleXU=0 Radius=1
    g7: BSplineCurve PolesCount=3 KnotsCount=2 Degree=2 IsPeriodic=0
    g8: GeomPoint X=175.022 Y=27.0628 Z=0
    g9: GeomPoint X=179.022 Y=27.0628 Z=0
    g10: Circle CenterX=189.124 CenterY=27.0628 CenterZ=0 NormalX=0 NormalY=0 NormalZ=1 AngleXU=0 Radius=1
    g11: Circle CenterX=185.124 CenterY=24.8665 CenterZ=0 NormalX=0 NormalY=0 NormalZ=1 AngleXU=0 Radius=1
    g12: Circle CenterX=185.124 CenterY=27.0628 CenterZ=0 NormalX=0 NormalY=0 NormalZ=1 AngleXU=0 Radius=1
    g13: BSplineCurve PolesCount=3 KnotsCount=2 Degree=2 IsPeriodic=0
    g14: GeomPoint X=189.124 Y=27.0628 Z=0
    g15: GeomPoint X=185.124 Y=27.0628 Z=0
    g16: Circle CenterX=175.022 CenterY=5.37834 CenterZ=0 NormalX=0 NormalY=0 NormalZ=1 AngleXU=0 Radius=1
    g17: Circle CenterX=179.022 CenterY=7.57463 CenterZ=0 NormalX=0 NormalY=0 NormalZ=1 AngleXU=0 Radius=1
    g18: Circle CenterX=179.022 CenterY=5.34704 CenterZ=0 NormalX=0 NormalY=0 NormalZ=1 AngleXU=0 Radius=1
    g19: BSplineCurve PolesCount=3 KnotsCount=2 Degree=2 IsPeriodic=0
    g20: GeomPoint X=175.022 Y=5.37834 Z=0
    g21: GeomPoint X=179.022 Y=5.34704 Z=0
    g22: Circle CenterX=189.124 CenterY=5.37834 CenterZ=0 NormalX=0 NormalY=0 NormalZ=1 AngleXU=0 Radius=1
    g23: Circle CenterX=185.124 CenterY=7.57463 CenterZ=0 NormalX=0 NormalY=0 NormalZ=1 AngleXU=0 Radius=1
    g24: Circle CenterX=185.124 CenterY=5.34704 CenterZ=0 NormalX=0 NormalY=0 NormalZ=1 AngleXU=0 Radius=1
    g25: BSplineCurve PolesCount=3 KnotsCount=2 Degree=2 IsPeriodic=0
    g26: GeomPoint X=189.124 Y=5.37834 Z=0
    g27: GeomPoint X=185.124 Y=5.34704 Z=0
    g28: Circle CenterX=165.871 CenterY=18.1458 CenterZ=0 NormalX=0 NormalY=0 NormalZ=1 AngleXU=0 Radius=1
    g29: Circle CenterX=169.377 CenterY=16.2206 CenterZ=0 NormalX=0 NormalY=0 NormalZ=1 AngleXU=0 Radius=1
    g30: Circle CenterX=165.871 CenterY=14.2954 CenterZ=0 NormalX=0 NormalY=0 NormalZ=1 AngleXU=0 Radius=1
    g31: BSplineCurve PolesCount=3 KnotsCount=2 Degree=2 IsPeriodic=0
    g32: GeomPoint X=165.871 Y=18.1458 Z=0
    g33: GeomPoint X=165.871 Y=14.2954 Z=0
    g34: Circle CenterX=198.275 CenterY=18.1458 CenterZ=0 NormalX=0 NormalY=0 NormalZ=1 AngleXU=0 Radius=1
    g35: Circle CenterX=194.768 CenterY=16.2206 CenterZ=0 NormalX=0 NormalY=0 NormalZ=1 AngleXU=0 Radius=1
    g36: Circle CenterX=198.275 CenterY=14.2954 CenterZ=0 NormalX=0 NormalY=0 NormalZ=1 AngleXU=0 Radius=1
    g37: BSplineCurve PolesCount=3 KnotsCount=2 Degree=2 IsPeriodic=0
    g38: GeomPoint X=198.275 Y=18.1458 Z=0
    g39: GeomPoint X=198.275 Y=14.2954 Z=0
    g40: LineSegment StartX=407.073 StartY=-103.779 StartZ=0 EndX=-42.9272 EndY=-103.779 EndZ=0
    g41: Circle CenterX=125.607 CenterY=54.1951 CenterZ=0 NormalX=0 NormalY=0 NormalZ=1 AngleXU=0 Radius=1
    g42: Circle CenterX=139.632 CenterY=46.4944 CenterZ=0 NormalX=0 NormalY=0 NormalZ=1 AngleXU=0 Radius=1
    g43: Circle CenterX=127.326 CenterY=56.7187 CenterZ=0 NormalX=0 NormalY=0 NormalZ=1 AngleXU=0 Radius=1
    g44: BSplineCurve PolesCount=3 KnotsCount=2 Degree=2 IsPeriodic=0
    g45: GeomPoint X=125.607 Y=54.1951 Z=0
    g46: GeomPoint X=127.326 Y=56.7187 Z=0
    g47: Circle CenterX=236.821 CenterY=56.7187 CenterZ=0 NormalX=0 NormalY=0 NormalZ=1 AngleXU=0 Radius=1
    g48: Circle CenterX=224.513 CenterY=46.4944 CenterZ=0 NormalX=0 NormalY=0 NormalZ=1 AngleXU=0 Radius=1
    g49: Circle CenterX=238.538 CenterY=54.1951 CenterZ=0 NormalX=0 NormalY=0 NormalZ=1 AngleXU=0 Radius=1
    g50: BSplineCurve PolesCount=3 KnotsCount=2 Degree=2 IsPeriodic=0
    g51: GeomPoint X=236.821 Y=56.7187 Z=0
    g52: GeomPoint X=238.538 Y=54.1951 Z=0
    g53: Circle CenterX=238.538 CenterY=-21.7539 CenterZ=0 NormalX=0 NormalY=0 NormalZ=1 AngleXU=0 Radius=1
    g54: Circle CenterX=224.513 CenterY=-14.0532 CenterZ=0 NormalX=0 NormalY=0 NormalZ=1 AngleXU=0 Radius=1
    g55: Circle CenterX=236.821 CenterY=-24.2775 CenterZ=0 NormalX=0 NormalY=0 NormalZ=1 AngleXU=0 Radius=1
    g56: BSplineCurve PolesCount=3 KnotsCount=2 Degree=2 IsPeriodic=0
    g57: GeomPoint X=238.538 Y=-21.7539 Z=0
    g58: GeomPoint X=236.821 Y=-24.2775 Z=0
    g59: Circle CenterX=125.607 CenterY=-21.7539 CenterZ=0 NormalX=0 NormalY=0 NormalZ=1 AngleXU=0 Radius=1
    g60: Circle CenterX=139.632 CenterY=-14.0532 CenterZ=0 NormalX=0 NormalY=0 NormalZ=1 AngleXU=0 Radius=1
    g61: Circle CenterX=127.325 CenterY=-24.2775 CenterZ=0 NormalX=0 NormalY=0 NormalZ=1 AngleXU=0 Radius=1
    g62: BSplineCurve PolesCount=3 KnotsCount=2 Degree=2 IsPeriodic=0
    g63: GeomPoint X=125.607 Y=-21.7539 Z=0
    g64: GeomPoint X=127.325 Y=-24.2775 Z=0
    g65: Circle CenterX=302.996 CenterY=111.695 CenterZ=0 NormalX=0 NormalY=0 NormalZ=1 AngleXU=0 Radius=1
    g66: Circle CenterX=306.073 CenterY=114.251 CenterZ=0 NormalX=0 NormalY=0 NormalZ=1 AngleXU=0 Radius=1
    g67: Circle CenterX=306.073 CenterY=110.251 CenterZ=0 NormalX=0 NormalY=0 NormalZ=1 AngleXU=0 Radius=1
    g68: BSplineCurve PolesCount=3 KnotsCount=2 Degree=2 IsPeriodic=0
    g69: GeomPoint X=302.996 Y=111.695 Z=0
    g70: GeomPoint X=306.073 Y=110.251 Z=0
    g71: Circle CenterX=306.073 CenterY=95.2763 CenterZ=0 NormalX=0 NormalY=0 NormalZ=1 AngleXU=0 Radius=1
    g72: Circle CenterX=306.073 CenterY=91.2763 CenterZ=0 NormalX=0 NormalY=0 NormalZ=1 AngleXU=0 Radius=1
    g73: Circle CenterX=302.567 CenterY=89.3511 CenterZ=0 NormalX=0 NormalY=0 NormalZ=1 AngleXU=0 Radius=1
    g74: BSplineCurve PolesCount=3 KnotsCount=2 Degree=2 IsPeriodic=0
    g75: GeomPoint X=306.073 Y=95.2763 Z=0
    g76: GeomPoint X=302.567 Y=89.3511 Z=0
    g77: LineSegment StartX=306.073 StartY=110.251 StartZ=0 EndX=306.073 EndY=95.2763 EndZ=0
    g78: LineSegment StartX=302.996 StartY=111.695 StartZ=0 EndX=236.821 EndY=56.7187 EndZ=0
    g79: LineSegment StartX=238.538 StartY=54.1951 StartZ=0 EndX=302.567 EndY=89.3511 EndZ=0
    g80: Circle CenterX=61.1496 CenterY=111.695 CenterZ=0 NormalX=0 NormalY=0 NormalZ=1 AngleXU=0 Radius=1
    g81: Circle CenterX=58.0728 CenterY=114.251 CenterZ=0 NormalX=0 NormalY=0 NormalZ=1 AngleXU=0 Radius=1
    g82: Circle CenterX=58.0728 CenterY=110.251 CenterZ=0 NormalX=0 NormalY=0 NormalZ=1 AngleXU=0 Radius=1
    g83: BSplineCurve PolesCount=3 KnotsCount=2 Degree=2 IsPeriodic=0
    g84: GeomPoint X=61.1496 Y=111.695 Z=0
    g85: GeomPoint X=58.0728 Y=110.251 Z=0
    g86: Circle CenterX=61.5791 CenterY=89.3511 CenterZ=0 NormalX=0 NormalY=0 NormalZ=1 AngleXU=0 Radius=1
    g87: Circle CenterX=58.0728 CenterY=91.2763 CenterZ=0 NormalX=0 NormalY=0 NormalZ=1 AngleXU=0 Radius=1
    g88: Circle CenterX=58.0728 CenterY=95.2763 CenterZ=0 NormalX=0 NormalY=0 NormalZ=1 AngleXU=0 Radius=1
    g89: BSplineCurve PolesCount=3 KnotsCount=2 Degree=2 IsPeriodic=0
    g90: GeomPoint X=61.5791 Y=89.3511 Z=0
    g91: GeomPoint X=58.0728 Y=95.2763 Z=0
    g92: LineSegment StartX=58.0728 StartY=110.251 StartZ=0 EndX=58.0728 EndY=95.2763 EndZ=0
    g93: LineSegment StartX=61.1496 StartY=111.695 StartZ=0 EndX=127.326 EndY=56.7187 EndZ=0
    g94: LineSegment StartX=125.607 StartY=54.1951 StartZ=0 EndX=61.5791 EndY=89.3511 EndZ=0
    g95: Circle CenterX=61.5791 CenterY=-56.9099 CenterZ=0 NormalX=0 NormalY=0 NormalZ=1 AngleXU=0 Radius=1
    g96: Circle CenterX=58.0728 CenterY=-58.8351 CenterZ=0 NormalX=0 NormalY=0 NormalZ=1 AngleXU=0 Radius=1
    g97: Circle CenterX=58.0728 CenterY=-62.8351 CenterZ=0 NormalX=0 NormalY=0 NormalZ=1 AngleXU=0 Radius=1
    g98: BSplineCurve PolesCount=3 KnotsCount=2 Degree=2 IsPeriodic=0
    g99: GeomPoint X=61.5791 Y=-56.9099 Z=0
    g100: GeomPoint X=58.0728 Y=-62.8351 Z=0
    g101: Circle CenterX=58.0728 CenterY=-77.8102 CenterZ=0 NormalX=0 NormalY=0 NormalZ=1 AngleXU=0 Radius=1
    g102: Circle CenterX=58.0728 CenterY=-81.8102 CenterZ=0 NormalX=0 NormalY=0 NormalZ=1 AngleXU=0 Radius=1
    g103: Circle CenterX=61.1496 CenterY=-79.2541 CenterZ=0 NormalX=0 NormalY=0 NormalZ=1 AngleXU=0 Radius=1
    g104: BSplineCurve PolesCount=3 KnotsCount=2 Degree=2 IsPeriodic=0
    g105: GeomPoint X=58.0728 Y=-77.8102 Z=0
    g106: GeomPoint X=61.1496 Y=-79.2541 Z=0
    g107: LineSegment StartX=58.0728 StartY=-62.8351 StartZ=0 EndX=58.0728 EndY=-77.8102 EndZ=0
    g108: LineSegment StartX=61.1496 StartY=-79.2541 StartZ=0 EndX=127.325 EndY=-24.2775 EndZ=0
    g109: LineSegment StartX=125.607 StartY=-21.7539 StartZ=0 EndX=61.5791 EndY=-56.9099 EndZ=0
    g110: Circle CenterX=302.567 CenterY=-56.9099 CenterZ=0 NormalX=0 NormalY=0 NormalZ=1 AngleXU=0 Radius=1
    g111: Circle CenterX=306.073 CenterY=-58.8351 CenterZ=0 NormalX=0 NormalY=0 NormalZ=1 AngleXU=0 Radius=1
    g112: Circle CenterX=306.073 CenterY=-62.8351 CenterZ=0 NormalX=0 NormalY=0 NormalZ=1 AngleXU=0 Radius=1
    g113: BSplineCurve PolesCount=3 KnotsCount=2 Degree=2 IsPeriodic=0
    g114: GeomPoint X=302.567 Y=-56.9099 Z=0
    g115: GeomPoint X=306.073 Y=-62.8351 Z=0
    g116: Circle CenterX=302.996 CenterY=-79.2541 CenterZ=0 NormalX=0 NormalY=0 NormalZ=1 AngleXU=0 Radius=1
    g117: Circle CenterX=306.073 CenterY=-81.8102 CenterZ=0 NormalX=0 NormalY=0 NormalZ=1 AngleXU=0 Radius=1
    g118: Circle CenterX=306.073 CenterY=-77.8102 CenterZ=0 NormalX=0 NormalY=0 NormalZ=1 AngleXU=0 Radius=1
    g119: BSplineCurve PolesCount=3 KnotsCount=2 Degree=2 IsPeriodic=0
    g120: GeomPoint X=302.996 Y=-79.2541 Z=0
    g121: GeomPoint X=306.073 Y=-77.8102 Z=0
    g122: LineSegment StartX=306.073 StartY=-62.8351 StartZ=0 EndX=306.073 EndY=-77.8102 EndZ=0
    g123: LineSegment StartX=302.996 StartY=-79.2541 StartZ=0 EndX=236.821 EndY=-24.2775 EndZ=0
    g124: LineSegment StartX=238.538 StartY=-21.7539 StartZ=0 EndX=302.567 EndY=-56.9099 EndZ=0
    g125: Circle CenterX=61.6457 CenterY=-88.8112 CenterZ=0 NormalX=0 NormalY=0 NormalZ=1 AngleXU=0 Radius=1
    g126: Circle CenterX=58.0728 CenterY=-91.7794 CenterZ=0 NormalX=0 NormalY=0 NormalZ=1 AngleXU=0 Radius=1
    g127: Circle CenterX=63.9135 CenterY=-91.7791 CenterZ=0 NormalX=0 NormalY=0 NormalZ=1 AngleXU=0 Radius=1
    g128: BSplineCurve PolesCount=3 KnotsCount=2 Degree=2 IsPeriodic=0
    g129: GeomPoint X=61.6457 Y=-88.8112 Z=0
    g130: GeomPoint X=63.9135 Y=-91.7791 Z=0
    g131: Circle CenterX=179.022 CenterY=-85.8163 CenterZ=0 NormalX=0 NormalY=0 NormalZ=1 AngleXU=0 Radius=1
    g132: Circle CenterX=179.022 CenterY=-91.7794 CenterZ=0 NormalX=0 NormalY=0 NormalZ=1 AngleXU=0 Radius=1
    g133: Circle CenterX=171.895 CenterY=-91.7791 CenterZ=0 NormalX=0 NormalY=0 NormalZ=1 AngleXU=0 Radius=1
    g134: BSplineCurve PolesCount=3 KnotsCount=2 Degree=2 IsPeriodic=0
    g135: GeomPoint X=179.022 Y=-85.8163 Z=0
    g136: GeomPoint X=171.895 Y=-91.7791 Z=0
    g137: Circle CenterX=185.124 CenterY=-86.2028 CenterZ=0 NormalX=0 NormalY=0 NormalZ=1 AngleXU=0 Radius=1
    g138: Circle CenterX=185.124 CenterY=-91.7794 CenterZ=0 NormalX=0 NormalY=0 NormalZ=1 AngleXU=0 Radius=1
    g139: Circle CenterX=191.747 CenterY=-91.7794 CenterZ=0 NormalX=0 NormalY=0 NormalZ=1 AngleXU=0 Radius=1
    g140: BSplineCurve PolesCount=3 KnotsCount=2 Degree=2 IsPeriodic=0
    g141: GeomPoint X=185.124 Y=-86.2028 Z=0
    g142: GeomPoint X=191.747 Y=-91.7794 Z=0
    g143: Circle CenterX=299.888 CenterY=-86.6413 CenterZ=0 NormalX=0 NormalY=0 NormalZ=1 AngleXU=0 Radius=1
    g144: Circle CenterX=306.073 CenterY=-91.7794 CenterZ=0 NormalX=0 NormalY=0 NormalZ=1 AngleXU=0 Radius=1
    g145: Circle CenterX=298.776 CenterY=-91.7794 CenterZ=0 NormalX=0 NormalY=0 NormalZ=1 AngleXU=0 Radius=1
    g146: BSplineCurve PolesCount=3 KnotsCount=2 Degree=2 IsPeriodic=0
    g147: GeomPoint X=299.888 Y=-86.6413 Z=0
    g148: GeomPoint X=298.776 Y=-91.7794 Z=0
    g149: LineSegment StartX=189.124 StartY=5.37834 StartZ=0 EndX=299.888 EndY=-86.6413 EndZ=0
    g150: LineSegment StartX=298.776 StartY=-91.7794 StartZ=0 EndX=191.747 EndY=-91.7794 EndZ=0
    g151: LineSegment StartX=185.124 StartY=-86.2028 StartZ=0 EndX=185.124 EndY=5.34704 EndZ=0
    g152: LineSegment StartX=179.022 StartY=5.34704 StartZ=0 EndX=179.022 EndY=-85.8163 EndZ=0
    g153: LineSegment StartX=171.895 StartY=-91.7791 StartZ=0 EndX=63.9135 EndY=-91.7791 EndZ=0
    g154: LineSegment StartX=61.6457 StartY=-88.8112 StartZ=0 EndX=175.022 EndY=5.37834 EndZ=0
    g155: Circle CenterX=302.073 CenterY=124.221 CenterZ=0 NormalX=0 NormalY=0 NormalZ=1 AngleXU=0 Radius=1
    g156: Circle CenterX=306.073 CenterY=124.221 CenterZ=0 NormalX=0 NormalY=0 NormalZ=1 AngleXU=0 Radius=1
    g157: Circle CenterX=302.996 CenterY=121.665 CenterZ=0 NormalX=0 NormalY=0 NormalZ=1 AngleXU=0 Radius=1
    g158: BSplineCurve PolesCount=3 KnotsCount=2 Degree=2 IsPeriodic=0
    g159: GeomPoint X=302.073 Y=124.221 Z=0
    g160: GeomPoint X=302.996 Y=121.665 Z=0
    g161: Circle CenterX=189.124 CenterY=124.221 CenterZ=0 NormalX=0 NormalY=0 NormalZ=1 AngleXU=0 Radius=1
    g162: Circle CenterX=185.124 CenterY=124.221 CenterZ=0 NormalX=0 NormalY=0 NormalZ=1 AngleXU=0 Radius=1
    g163: Circle CenterX=185.124 CenterY=120.221 CenterZ=0 NormalX=0 NormalY=0 NormalZ=1 AngleXU=0 Radius=1
    g164: BSplineCurve PolesCount=3 KnotsCount=2 Degree=2 IsPeriodic=0
    g165: GeomPoint X=189.124 Y=124.221 Z=0
    g166: GeomPoint X=185.124 Y=120.221 Z=0
    g167: Circle CenterX=175.022 CenterY=124.221 CenterZ=0 NormalX=0 NormalY=0 NormalZ=1 AngleXU=0 Radius=1
    g168: Circle CenterX=179.022 CenterY=124.221 CenterZ=0 NormalX=0 NormalY=0 NormalZ=1 AngleXU=0 Radius=1
    g169: Circle CenterX=179.022 CenterY=120.221 CenterZ=0 NormalX=0 NormalY=0 NormalZ=1 AngleXU=0 Radius=1
    g170: BSplineCurve PolesCount=3 KnotsCount=2 Degree=2 IsPeriodic=0
    g171: GeomPoint X=175.022 Y=124.221 Z=0
    g172: GeomPoint X=179.022 Y=120.221 Z=0
    g173: Circle CenterX=62.0728 CenterY=124.221 CenterZ=0 NormalX=0 NormalY=0 NormalZ=1 AngleXU=0 Radius=1
    g174: Circle CenterX=58.0728 CenterY=124.221 CenterZ=0 NormalX=0 NormalY=0 NormalZ=1 AngleXU=0 Radius=1
    g175: Circle CenterX=61.1496 CenterY=121.665 CenterZ=0 NormalX=0 NormalY=0 NormalZ=1 AngleXU=0 Radius=1
    g176: BSplineCurve PolesCount=3 KnotsCount=2 Degree=2 IsPeriodic=0
    g177: GeomPoint X=62.0728 Y=124.221 Z=0
    g178: GeomPoint X=61.1496 Y=121.665 Z=0
    g179: LineSegment StartX=179.022 StartY=120.221 StartZ=0 EndX=179.022 EndY=27.0628 EndZ=0
    g180: LineSegment StartX=185.124 StartY=27.0628 StartZ=0 EndX=185.124 EndY=120.221 EndZ=0
    g181: LineSegment StartX=302.996 StartY=121.665 StartZ=0 EndX=189.124 EndY=27.0628 EndZ=0
    g182: LineSegment StartX=175.022 StartY=27.0628 StartZ=0 EndX=61.1496 EndY=121.665 EndZ=0
    g183: Circle CenterX=61.5791 CenterY=75.4095 CenterZ=0 NormalX=0 NormalY=0 NormalZ=1 AngleXU=0 Radius=1
    g184: Circle CenterX=58.0728 CenterY=77.3346 CenterZ=0 NormalX=0 NormalY=0 NormalZ=1 AngleXU=0 Radius=1
    g185: Circle CenterX=58.0728 CenterY=73.3346 CenterZ=0 NormalX=0 NormalY=0 NormalZ=1 AngleXU=0 Radius=1
    g186: BSplineCurve PolesCount=3 KnotsCount=2 Degree=2 IsPeriodic=0
    g187: GeomPoint X=61.5791 Y=75.4095 Z=0
    g188: GeomPoint X=58.0728 Y=73.3346 Z=0
    g189: Circle CenterX=58.0728 CenterY=-40.8935 CenterZ=0 NormalX=0 NormalY=0 NormalZ=1 AngleXU=0 Radius=1
    g190: Circle CenterX=58.0728 CenterY=-44.8935 CenterZ=0 NormalX=0 NormalY=0 NormalZ=1 AngleXU=0 Radius=1
    g191: Circle CenterX=61.5791 CenterY=-42.9683 CenterZ=0 NormalX=0 NormalY=0 NormalZ=1 AngleXU=0 Radius=1
    g192: BSplineCurve PolesCount=3 KnotsCount=2 Degree=2 IsPeriodic=0
    g193: GeomPoint X=58.0728 Y=-40.8935 Z=0
    g194: GeomPoint X=61.5791 Y=-42.9683 Z=0
    g195: LineSegment StartX=61.5791 StartY=-42.9683 StartZ=0 EndX=165.871 EndY=14.2954 EndZ=0
    g196: LineSegment StartX=165.871 StartY=18.1458 StartZ=0 EndX=61.5791 EndY=75.4095 EndZ=0
    g197: LineSegment StartX=58.0728 StartY=73.3346 StartZ=0 EndX=58.0728 EndY=-40.8935 EndZ=0
    g198: Circle CenterX=302.567 CenterY=-42.9683 CenterZ=0 NormalX=0 NormalY=0 NormalZ=1 AngleXU=0 Radius=1
    g199: Circle CenterX=306.073 CenterY=-44.8935 CenterZ=0 NormalX=0 NormalY=0 NormalZ=1 AngleXU=0 Radius=1
    g200: Circle CenterX=306.073 CenterY=-40.8935 CenterZ=0 NormalX=0 NormalY=0 NormalZ=1 AngleXU=0 Radius=1
    g201: BSplineCurve PolesCount=3 KnotsCount=2 Degree=2 IsPeriodic=0
    g202: GeomPoint X=302.567 Y=-42.9683 Z=0
    g203: GeomPoint X=306.073 Y=-40.8935 Z=0
    g204: Circle CenterX=306.073 CenterY=73.3346 CenterZ=0 NormalX=0 NormalY=0 NormalZ=1 AngleXU=0 Radius=1
    g205: Circle CenterX=306.073 CenterY=77.3346 CenterZ=0 NormalX=0 NormalY=0 NormalZ=1 AngleXU=0 Radius=1
    g206: Circle CenterX=302.567 CenterY=75.4095 CenterZ=0 NormalX=0 NormalY=0 NormalZ=1 AngleXU=0 Radius=1
    g207: BSplineCurve PolesCount=3 KnotsCount=2 Degree=2 IsPeriodic=0
    g208: GeomPoint X=306.073 Y=73.3346 Z=0
    g209: GeomPoint X=302.567 Y=75.4095 Z=0
    g210: LineSegment StartX=302.567 StartY=-42.9683 StartZ=0 EndX=198.275 EndY=14.2954 EndZ=0
    g211: LineSegment StartX=198.275 StartY=18.1458 StartZ=0 EndX=302.567 EndY=75.4095 EndZ=0
    g212: LineSegment StartX=306.073 StartY=73.3346 StartZ=0 EndX=306.073 EndY=-40.8935 EndZ=0
    g213: LineSegment StartX=322.073 StartY=105.865 StartZ=0 EndX=328.643 EndY=105.865 EndZ=0
    g214: LineSegment StartX=318.073 StartY=120.221 StartZ=0 EndX=318.073 EndY=109.865 EndZ=0
    g215: LineSegment StartX=336.157 StartY=107.779 StartZ=0 EndX=362.567 EndY=122.294 EndZ=0
    g216: Circle CenterX=362.073 CenterY=124.221 CenterZ=0 NormalX=0 NormalY=0 NormalZ=1 AngleXU=0 Radius=1
    g217: Circle CenterX=366.073 CenterY=124.221 CenterZ=0 NormalX=0 NormalY=0 NormalZ=1 AngleXU=0 Radius=1
    g218: Circle CenterX=362.567 CenterY=122.294 CenterZ=0 NormalX=0 NormalY=0 NormalZ=1 AngleXU=0 Radius=1
    g219: BSplineCurve PolesCount=3 KnotsCount=2 Degree=2 IsPeriodic=0
    g220: GeomPoint X=362.073 Y=124.221 Z=0
    g221: GeomPoint X=362.567 Y=122.294 Z=0
    g222: Circle CenterX=322.073 CenterY=124.221 CenterZ=0 NormalX=0 NormalY=0 NormalZ=1 AngleXU=0 Radius=1
    g223: Circle CenterX=318.073 CenterY=124.221 CenterZ=0 NormalX=0 NormalY=0 NormalZ=1 AngleXU=0 Radius=1
    g224: Circle CenterX=318.073 CenterY=120.221 CenterZ=0 NormalX=0 NormalY=0 NormalZ=1 AngleXU=0 Radius=1
    g225: BSplineCurve PolesCount=3 KnotsCount=2 Degree=2 IsPeriodic=0
    g226: GeomPoint X=322.073 Y=124.221 Z=0
    g227: GeomPoint X=318.073 Y=120.221 Z=0
    g228: Circle CenterX=322.073 CenterY=105.865 CenterZ=0 NormalX=0 NormalY=0 NormalZ=1 AngleXU=0 Radius=1
    g229: Circle CenterX=318.073 CenterY=105.865 CenterZ=0 NormalX=0 NormalY=0 NormalZ=1 AngleXU=0 Radius=1
    g230: Circle CenterX=318.073 CenterY=109.865 CenterZ=0 NormalX=0 NormalY=0 NormalZ=1 AngleXU=0 Radius=1
    g231: BSplineCurve PolesCount=3 KnotsCount=2 Degree=2 IsPeriodic=0
    g232: GeomPoint X=322.073 Y=105.865 Z=0
    g233: GeomPoint X=318.073 Y=109.865 Z=0
    g234: Circle CenterX=336.157 CenterY=107.779 CenterZ=0 NormalX=0 NormalY=0 NormalZ=1 AngleXU=0 Radius=1
    g235: Circle CenterX=332.651 CenterY=105.853 CenterZ=0 NormalX=0 NormalY=0 NormalZ=1 AngleXU=0 Radius=1
    g236: Circle CenterX=328.643 CenterY=105.865 CenterZ=0 NormalX=0 NormalY=0 NormalZ=1 AngleXU=0 Radius=1
    g237: BSplineCurve PolesCount=3 KnotsCount=2 Degree=2 IsPeriodic=0
    g238: GeomPoint X=336.157 Y=107.779 Z=0
    g239: GeomPoint X=328.643 Y=105.865 Z=0
    g240: LineSegment StartX=322.073 StartY=124.221 StartZ=0 EndX=362.073 EndY=124.221 EndZ=0
    g241: Circle CenterX=371.567 CenterY=-80.8644 CenterZ=0 NormalX=0 NormalY=0 NormalZ=1 AngleXU=0 Radius=1
    g242: Circle CenterX=375.073 CenterY=-82.7896 CenterZ=0 NormalX=0 NormalY=0 NormalZ=1 AngleXU=0 Radius=1
    g243: Circle CenterX=375.073 CenterY=-78.7896 CenterZ=0 NormalX=0 NormalY=0 NormalZ=1 AngleXU=0 Radius=1
    g244: BSplineCurve PolesCount=3 KnotsCount=2 Degree=2 IsPeriodic=0
    g245: GeomPoint X=371.567 Y=-80.8644 Z=0
    g246: GeomPoint X=375.073 Y=-78.7896 Z=0
    g247: Circle CenterX=321.579 CenterY=-53.4075 CenterZ=0 NormalX=0 NormalY=0 NormalZ=1 AngleXU=0 Radius=1
    g248: Circle CenterX=318.073 CenterY=-51.4823 CenterZ=0 NormalX=0 NormalY=0 NormalZ=1 AngleXU=0 Radius=1
    g249: Circle CenterX=318.073 CenterY=-47.4805 CenterZ=0 NormalX=0 NormalY=0 NormalZ=1 AngleXU=0 Radius=1
    g250: BSplineCurve PolesCount=3 KnotsCount=2 Degree=2 IsPeriodic=0
    g251: GeomPoint X=321.579 Y=-53.4075 Z=0
    g252: GeomPoint X=318.073 Y=-47.4805 Z=0
    g253: LineSegment StartX=371.567 StartY=-80.8644 StartZ=0 EndX=321.579 EndY=-53.4075 EndZ=0
    g254: Circle CenterX=321.579 CenterY=-67.3492 CenterZ=0 NormalX=0 NormalY=0 NormalZ=1 AngleXU=0 Radius=1
    g255: Circle CenterX=318.073 CenterY=-65.424 CenterZ=0 NormalX=0 NormalY=0 NormalZ=1 AngleXU=0 Radius=1
    g256: Circle CenterX=318.073 CenterY=-69.424 CenterZ=0 NormalX=0 NormalY=0 NormalZ=1 AngleXU=0 Radius=1
    g257: BSplineCurve PolesCount=3 KnotsCount=2 Degree=2 IsPeriodic=0
    g258: GeomPoint X=321.579 Y=-67.3492 Z=0
    g259: GeomPoint X=318.073 Y=-69.424 Z=0
    g260: Circle CenterX=362.567 CenterY=-89.8542 CenterZ=0 NormalX=0 NormalY=0 NormalZ=1 AngleXU=0 Radius=1
    g261: Circle CenterX=366.073 CenterY=-91.7794 CenterZ=0 NormalX=0 NormalY=0 NormalZ=1 AngleXU=0 Radius=1
    g262: Circle CenterX=362.073 CenterY=-91.7794 CenterZ=0 NormalX=0 NormalY=0 NormalZ=1 AngleXU=0 Radius=1
    g263: BSplineCurve PolesCount=3 KnotsCount=2 Degree=2 IsPeriodic=0
    g264: GeomPoint X=362.567 Y=-89.8542 Z=0
    g265: GeomPoint X=362.073 Y=-91.7794 Z=0
    g266: Circle CenterX=322.073 CenterY=-91.7794 CenterZ=0 NormalX=0 NormalY=0 NormalZ=1 AngleXU=0 Radius=1
    g267: Circle CenterX=318.073 CenterY=-91.7794 CenterZ=0 NormalX=0 NormalY=0 NormalZ=1 AngleXU=0 Radius=1
    g268: Circle CenterX=318.073 CenterY=-87.7794 CenterZ=0 NormalX=0 NormalY=0 NormalZ=1 AngleXU=0 Radius=1
    g269: BSplineCurve PolesCount=3 KnotsCount=2 Degree=2 IsPeriodic=0
    g270: GeomPoint X=322.073 Y=-91.7794 Z=0
    g271: GeomPoint X=318.073 Y=-87.7794 Z=0
    g272: LineSegment StartX=362.567 StartY=-89.8542 StartZ=0 EndX=321.579 EndY=-67.3492 EndZ=0
    g273: LineSegment StartX=318.073 StartY=-69.424 StartZ=0 EndX=318.073 EndY=-87.7794 EndZ=0
    g274: LineSegment StartX=322.073 StartY=-91.7794 StartZ=0 EndX=362.073 EndY=-91.7794 EndZ=0
    g275: Circle CenterX=2.07281 CenterY=124.221 CenterZ=0 NormalX=0 NormalY=0 NormalZ=1 AngleXU=0 Radius=1
    g276: Circle CenterX=1.57905 CenterY=122.295 CenterZ=0 NormalX=0 NormalY=0 NormalZ=1 AngleXU=0 Radius=1
    g277: BSplineCurve PolesCount=3 KnotsCount=2 Degree=2 IsPeriodic=0
    g278: GeomPoint X=2.07281 Y=124.221 Z=0
    g279: GeomPoint X=1.57905 Y=122.295 Z=0
    g280: Circle CenterX=42.0728 CenterY=124.221 CenterZ=0 NormalX=0 NormalY=0 NormalZ=1 AngleXU=0 Radius=1
    g281: Circle CenterX=46.0728 CenterY=124.221 CenterZ=0 NormalX=0 NormalY=0 NormalZ=1 AngleXU=0 Radius=1
    g282: Circle CenterX=46.0728 CenterY=120.221 CenterZ=0 NormalX=0 NormalY=0 NormalZ=1 AngleXU=0 Radius=1
    g283: BSplineCurve PolesCount=3 KnotsCount=2 Degree=2 IsPeriodic=0
    g284: GeomPoint X=42.0728 Y=124.221 Z=0
    g285: GeomPoint X=46.0728 Y=120.221 Z=0
    g286: Circle CenterX=46.0728 CenterY=109.865 CenterZ=0 NormalX=0 NormalY=0 NormalZ=1 AngleXU=0 Radius=1
    g287: Circle CenterX=46.0728 CenterY=105.865 CenterZ=0 NormalX=0 NormalY=0 NormalZ=1 AngleXU=0 Radius=1
    g288: Circle CenterX=42.0728 CenterY=105.865 CenterZ=0 NormalX=0 NormalY=0 NormalZ=1 AngleXU=0 Radius=1
    g289: BSplineCurve PolesCount=3 KnotsCount=2 Degree=2 IsPeriodic=0
    g290: GeomPoint X=46.0728 Y=109.865 Z=0
    g291: GeomPoint X=42.0728 Y=105.865 Z=0
    g292: Circle CenterX=35.5028 CenterY=105.865 CenterZ=0 NormalX=0 NormalY=0 NormalZ=1 AngleXU=0 Radius=1
    g293: Circle CenterX=31.5028 CenterY=105.865 CenterZ=0 NormalX=0 NormalY=0 NormalZ=1 AngleXU=0 Radius=1
    g294: Circle CenterX=27.9965 CenterY=107.79 CenterZ=0 NormalX=0 NormalY=0 NormalZ=1 AngleXU=0 Radius=1
    g295: BSplineCurve PolesCount=3 KnotsCount=2 Degree=2 IsPeriodic=0
    g296: GeomPoint X=35.5028 Y=105.865 Z=0
    g297: GeomPoint X=27.9965 Y=107.79 Z=0
    g298: LineSegment StartX=2.07281 StartY=124.221 StartZ=0 EndX=42.0728 EndY=124.221 EndZ=0
    g299: LineSegment StartX=46.0728 StartY=120.221 StartZ=0 EndX=46.0728 EndY=109.865 EndZ=0
    g300: LineSegment StartX=42.0728 StartY=105.865 StartZ=0 EndX=35.5028 EndY=105.865 EndZ=0
    g301: LineSegment StartX=27.9965 StartY=107.79 StartZ=0 EndX=1.57905 EndY=122.295 EndZ=0
    g302: Circle CenterX=42.5666 CenterY=-67.3492 CenterZ=0 NormalX=0 NormalY=0 NormalZ=1 AngleXU=0 Radius=1
    g303: Circle CenterX=46.0728 CenterY=-65.424 CenterZ=0 NormalX=0 NormalY=0 NormalZ=1 AngleXU=0 Radius=1
    g304: Circle CenterX=46.0728 CenterY=-69.424 CenterZ=0 NormalX=0 NormalY=0 NormalZ=1 AngleXU=0 Radius=1
    g305: BSplineCurve PolesCount=3 KnotsCount=2 Degree=2 IsPeriodic=0
    g306: GeomPoint X=42.5666 Y=-67.3492 Z=0
    g307: GeomPoint X=46.0728 Y=-69.424 Z=0
    g308: Circle CenterX=46.0728 CenterY=-87.7794 CenterZ=0 NormalX=0 NormalY=0 NormalZ=1 AngleXU=0 Radius=1
    g309: Circle CenterX=46.0728 CenterY=-91.7794 CenterZ=0 NormalX=0 NormalY=0 NormalZ=1 AngleXU=0 Radius=1
    g310: Circle CenterX=42.0728 CenterY=-91.7794 CenterZ=0 NormalX=0 NormalY=0 NormalZ=1 AngleXU=0 Radius=1
    g311: BSplineCurve PolesCount=3 KnotsCount=2 Degree=2 IsPeriodic=0
    g312: GeomPoint X=46.0728 Y=-87.7794 Z=0
    g313: GeomPoint X=42.0728 Y=-91.7794 Z=0
    g314: Circle CenterX=2.07281 CenterY=-91.7794 CenterZ=0 NormalX=0 NormalY=0 NormalZ=1 AngleXU=0 Radius=1
    g315: Circle CenterX=-1.92719 CenterY=-91.7794 CenterZ=0 NormalX=0 NormalY=0 NormalZ=1 AngleXU=0 Radius=1
    g316: Circle CenterX=1.57905 CenterY=-89.8542 CenterZ=0 NormalX=0 NormalY=0 NormalZ=1 AngleXU=0 Radius=1
    g317: BSplineCurve PolesCount=3 KnotsCount=2 Degree=2 IsPeriodic=0
    g318: GeomPoint X=2.07281 Y=-91.7794 Z=0
    g319: GeomPoint X=1.57905 Y=-89.8542 Z=0
    g320: LineSegment StartX=2.07281 StartY=-91.7794 StartZ=0 EndX=42.0728 EndY=-91.7794 EndZ=0
    g321: LineSegment StartX=46.0728 StartY=-87.7794 StartZ=0 EndX=46.0728 EndY=-69.424 EndZ=0
    g322: LineSegment StartX=42.5666 StartY=-67.3492 StartZ=0 EndX=1.57905 EndY=-89.8542 EndZ=0
    g323: Circle CenterX=322.073 CenterY=76.4095 CenterZ=0 NormalX=0 NormalY=0 NormalZ=1 AngleXU=0 Radius=4
    g324: BSplineCurve PolesCount=3 KnotsCount=2 Degree=2 IsPeriodic=0
    g325: GeomPoint X=318.073 Y=72.4095 Z=0
    g326: GeomPoint X=322.073 Y=76.4095 Z=0
    g327: Circle CenterX=375.073 CenterY=72.4095 CenterZ=0 NormalX=0 NormalY=0 NormalZ=1 AngleXU=0 Radius=1
    g328: Circle CenterX=375.073 CenterY=76.4095 CenterZ=0 NormalX=0 NormalY=0 NormalZ=1 AngleXU=0 Radius=1
    g329: Circle CenterX=371.073 CenterY=76.4095 CenterZ=0 NormalX=0 NormalY=0 NormalZ=1 AngleXU=0 Radius=1
    g330: BSplineCurve PolesCount=3 KnotsCount=2 Degree=2 IsPeriodic=0
    g331: GeomPoint X=375.073 Y=72.4095 Z=0
    g332: GeomPoint X=371.073 Y=76.4095 Z=0
    g333: LineSegment StartX=322.073 StartY=76.4095 StartZ=0 EndX=371.073 EndY=76.4095 EndZ=0
    g334: LineSegment StartX=318.073 StartY=72.4095 StartZ=0 EndX=318.073 EndY=-47.4805 EndZ=0
    g335: LineSegment StartX=375.073 StartY=72.4095 StartZ=0 EndX=375.073 EndY=-78.7896 EndZ=0
    g336: ArcOfCircle CenterX=-26.9272 CenterY=22.1087 CenterZ=0 NormalX=0 NormalY=0 NormalZ=1 AngleXU=0 Radius=4 StartAngle=5e-16 EndAngle=3.14159
    g337: LineSegment StartX=-22.9272 StartY=22.1087 StartZ=0 EndX=-18.9272 EndY=-83.7794 EndZ=0
    g338: LineSegment StartX=-34.9272 StartY=-83.7794 StartZ=0 EndX=-30.9272 EndY=22.1087 EndZ=0
    g339: ArcOfCircle CenterX=391.073 CenterY=22.1087 CenterZ=0 NormalX=0 NormalY=0 NormalZ=1 AngleXU=0 Radius=4 StartAngle=0 EndAngle=3.14159
    g340: LineSegment StartX=387.073 StartY=22.1087 StartZ=0 EndX=383.073 EndY=-83.7794 EndZ=0
    g341: LineSegment StartX=395.073 StartY=22.1087 StartZ=0 EndX=399.073 EndY=-83.7794 EndZ=0
    g342: Circle CenterX=-10.9272 CenterY=-78.7794 CenterZ=0 NormalX=0 NormalY=0 NormalZ=1 AngleXU=0 Radius=1
    g343: Circle CenterX=-10.9272 CenterY=-82.7794 CenterZ=0 NormalX=0 NormalY=0 NormalZ=1 AngleXU=0 Radius=1
    g344: Circle CenterX=-7.42095 CenterY=-80.8542 CenterZ=0 NormalX=0 NormalY=0 NormalZ=1 AngleXU=0 Radius=1
    g345: BSplineCurve PolesCount=3 KnotsCount=2 Degree=2 IsPeriodic=0
    g346: GeomPoint X=-10.9272 Y=-78.7794 Z=0
    g347: GeomPoint X=-7.42095 Y=-80.8542 Z=0
    g348: Circle CenterX=42.5666 CenterY=-53.4075 CenterZ=0 NormalX=0 NormalY=0 NormalZ=1 AngleXU=0 Radius=1
    g349: Circle CenterX=46.0728 CenterY=-51.4823 CenterZ=0 NormalX=0 NormalY=0 NormalZ=1 AngleXU=0 Radius=1
    g350: Circle CenterX=46.0728 CenterY=-47.4823 CenterZ=0 NormalX=0 NormalY=0 NormalZ=1 AngleXU=0 Radius=1
    g351: BSplineCurve PolesCount=3 KnotsCount=2 Degree=2 IsPeriodic=0
    g352: GeomPoint X=42.5666 Y=-53.4075 Z=0
    g353: GeomPoint X=46.0728 Y=-47.4823 Z=0
    g354: Circle CenterX=46.0728 CenterY=72.4095 CenterZ=0 NormalX=0 NormalY=0 NormalZ=1 AngleXU=0 Radius=1
    g355: Circle CenterX=46.0728 CenterY=76.4095 CenterZ=0 NormalX=0 NormalY=0 NormalZ=1 AngleXU=0 Radius=1
    g356: Circle CenterX=42.0728 CenterY=76.4095 CenterZ=0 NormalX=0 NormalY=0 NormalZ=1 AngleXU=0 Radius=1
    g357: BSplineCurve PolesCount=3 KnotsCount=2 Degree=2 IsPeriodic=0
    g358: GeomPoint X=46.0728 Y=72.4095 Z=0
    g359: GeomPoint X=42.0728 Y=76.4095 Z=0
    g360: Circle CenterX=-6.92718 CenterY=76.4095 CenterZ=0 NormalX=0 NormalY=0 NormalZ=1 AngleXU=0 Radius=1
    g361: Circle CenterX=-10.9272 CenterY=76.4095 CenterZ=0 NormalX=0 NormalY=0 NormalZ=1 AngleXU=0 Radius=1
    g362: Circle CenterX=-10.9272 CenterY=72.4095 CenterZ=0 NormalX=0 NormalY=0 NormalZ=1 AngleXU=0 Radius=1
    g363: BSplineCurve PolesCount=3 KnotsCount=2 Degree=2 IsPeriodic=0
    g364: GeomPoint X=-6.92718 Y=76.4095 Z=0
    g365: GeomPoint X=-10.9272 Y=72.4095 Z=0
    g366: LineSegment StartX=-10.9272 StartY=72.4095 StartZ=0 EndX=-10.9272 EndY=-78.7794 EndZ=0
    g367: LineSegment StartX=-7.42095 StartY=-80.8542 StartZ=0 EndX=42.5666 EndY=-53.4075 EndZ=0
    g368: LineSegment StartX=46.0728 StartY=-47.4823 StartZ=0 EndX=46.0728 EndY=72.4095 EndZ=0
    g369: LineSegment StartX=42.0728 StartY=76.4095 StartZ=0 EndX=-6.92719 EndY=76.4095 EndZ=0
    g370: LineSegment StartX=119.072 StartY=136.221 StartZ=0 EndX=119.072 EndY=-116.228 EndZ=0
    g371: LineSegment StartX=-42.9272 StartY=136.221 StartZ=0 EndX=407.073 EndY=136.221 EndZ=0
    g372: LineSegment StartX=232.072 StartY=136.221 StartZ=0 EndX=220.072 EndY=136.221 EndZ=0
    g373: LineSegment StartX=232.072 StartY=136.221 StartZ=0 EndX=232.072 EndY=124.221 EndZ=0
    g374: LineSegment StartX=220.072 StartY=136.221 StartZ=0 EndX=220.072 EndY=124.221 EndZ=0
    g375: LineSegment StartX=220.072 StartY=136.221 StartZ=0 EndX=226.072 EndY=136.221 EndZ=0
    g376: LineSegment StartX=220.072 StartY=136.221 StartZ=0 EndX=220.072 EndY=130.221 EndZ=0
    g377: LineSegment StartX=220.072 StartY=124.221 StartZ=0 EndX=226.072 EndY=124.221 EndZ=0
    g378: LineSegment StartX=232.072 StartY=124.221 StartZ=0 EndX=232.072 EndY=127.221 EndZ=0
    g379: LineSegment StartX=232.072 StartY=136.221 StartZ=0 EndX=232.072 EndY=133.221 EndZ=0
    g380-g384: Circle x5 (B-spline internal-alignment scaffolding for g385; pole/knot coordinates omitted)
    g385: BSplineCurve PolesCount=5 KnotsCount=3 Degree=3 IsPeriodic=0
    g386: GeomPoint X=232.072 Y=133.221 Z=0
    g387: GeomPoint X=223.072 Y=130.221 Z=0
    g388: GeomPoint X=232.072 Y=127.221 Z=0
    g389: LineSegment StartX=189.124 StartY=124.221 StartZ=0 EndX=302.073 EndY=124.221 EndZ=0
    g390: LineSegment StartX=132.072 StartY=136.221 StartZ=0 EndX=132.072 EndY=124.221 EndZ=0
    g391: LineSegment StartX=132.072 StartY=136.221 StartZ=0 EndX=144.072 EndY=136.221 EndZ=0
    g392: LineSegment StartX=144.072 StartY=136.221 StartZ=0 EndX=144.072 EndY=124.221 EndZ=0
    g393: LineSegment StartX=144.072 StartY=136.221 StartZ=0 EndX=138.072 EndY=136.221 EndZ=0
    g394: LineSegment StartX=144.072 StartY=136.221 StartZ=0 EndX=144.072 EndY=130.221 EndZ=0
    g395: LineSegment StartX=132.072 StartY=136.221 StartZ=0 EndX=132.072 EndY=133.221 EndZ=0
    g396: LineSegment StartX=132.072 StartY=133.221 StartZ=0 EndX=132.072 EndY=127.221 EndZ=0
    g397-g401: Circle x5 (B-spline internal-alignment scaffolding for g402; pole/knot coordinates omitted)
    g402: BSplineCurve PolesCount=5 KnotsCount=3 Degree=3 IsPeriodic=0
    g403: GeomPoint X=132.072 Y=133.221 Z=0
    g404: GeomPoint X=141.072 Y=130.221 Z=0
    g405: GeomPoint X=132.072 Y=127.221 Z=0
    g406: LineSegment StartX=132.072 StartY=124.221 StartZ=0 EndX=175.022 EndY=124.221 EndZ=0
    g407: LineSegment StartX=62.0728 StartY=124.221 StartZ=0 EndX=132.072 EndY=124.221 EndZ=0
    ... +15 more geometry lines
  constraints (717):
    c: Vertical(g0)
    c: Vertical(g1)
    c: Block(g1)
    c: Block(g0)
    c: Weight(g4) = 1
    c: Equal(g4,g5)
    c: Equal(g4,g6)
    c: InternalAlignment(g4,g7)
    c: InternalAlignment(g5,g7)
    c: InternalAlignment(g6,g7)
    c: InternalAlignment(g8,g7)
    c: InternalAlignment(g9,g7)
    c: Weight(g10) = 1
    c: Equal(g10,g11)
    c: Equal(g10,g12)
    c: InternalAlignment(g10,g13)
    c: InternalAlignment(g11,g13)
    c: InternalAlignment(g12,g13)
    c: InternalAlignment(g14,g13)
    c: InternalAlignment(g15,g13)
    c: Block(g13)
    c: Block(g7)
    c: Weight(g16) = 1
    c: Equal(g16,g17)
    c: Equal(g16,g18)
    c: InternalAlignment(g16,g19)
    c: InternalAlignment(g17,g19)
    c: InternalAlignment(g18,g19)
    c: InternalAlignment(g20,g19)
    c: InternalAlignment(g21,g19)
    c: Weight(g22) = 1
    c: Equal(g22,g23)
    c: Equal(g22,g24)
    c: InternalAlignment(g22,g25)
    c: InternalAlignment(g23,g25)
    c: InternalAlignment(g24,g25)
    c: InternalAlignment(g26,g25)
    c: InternalAlignment(g27,g25)
    c: Block(g25)
    c: Block(g19)
    c: Weight(g28) = 1
    c: Equal(g28,g29)
    c: Equal(g28,g30)
    c: InternalAlignment(g28,g31)
    c: InternalAlignment(g29,g31)
    c: InternalAlignment(g30,g31)
    c: InternalAlignment(g32,g31)
    c: InternalAlignment(g33,g31)
    c: Weight(g34) = 1
    c: Equal(g34,g35)
    c: Equal(g34,g36)
    c: InternalAlignment(g34,g37)
    c: InternalAlignment(g35,g37)
    c: InternalAlignment(g36,g37)
    c: InternalAlignment(g38,g37)
    c: InternalAlignment(g39,g37)
    c: Block(g31)
    c: Block(g37)
    c: Coincident(g40,g1)
    c: Coincident(g40,g0)
    c: Horizontal(g40)
    c: Distance(g40) = 450
    c: Weight(g41) = 1
    c: Equal(g41,g42)
    c: Equal(g41,g43)
    c: InternalAlignment(g41,g44)
    c: InternalAlignment(g42,g44)
    c: InternalAlignment(g43,g44)
    c: InternalAlignment(g45,g44)
    c: InternalAlignment(g46,g44)
    c: Block(g44)
    c: Weight(g47) = 1
    c: Equal(g47,g48)
    c: Equal(g47,g49)
    c: InternalAlignment(g47,g50)
    c: InternalAlignment(g48,g50)
    c: InternalAlignment(g49,g50)
    c: InternalAlignment(g51,g50)
    c: InternalAlignment(g52,g50)
    c: Block(g50)
    c: Weight(g53) = 1
    c: Equal(g53,g54)
    c: Equal(g53,g55)
    c: InternalAlignment(g53,g56)
    c: InternalAlignment(g54,g56)
    c: InternalAlignment(g55,g56)
    c: InternalAlignment(g57,g56)
    c: InternalAlignment(g58,g56)
    c: Block(g56)
    c: Weight(g59) = 1
    c: Equal(g59,g60)
    c: Equal(g59,g61)
    c: InternalAlignment(g59,g62)
    c: InternalAlignment(g60,g62)
    c: InternalAlignment(g61,g62)
    c: InternalAlignment(g63,g62)
    c: InternalAlignment(g64,g62)
    c: Block(g62)
    c: Weight(g65) = 1
    c: Equal(g65,g66)
    c: Equal(g65,g67)
    c: InternalAlignment(g65,g68)
    c: InternalAlignment(g66,g68)
    c: InternalAlignment(g67,g68)
    c: InternalAlignment(g69,g68)
    c: InternalAlignment(g70,g68)
    c: Weight(g71) = 1
    c: Equal(g71,g72)
    c: Equal(g71,g73)
    c: InternalAlignment(g71,g74)
    c: InternalAlignment(g72,g74)
    c: InternalAlignment(g73,g74)
    c: InternalAlignment(g75,g74)
    c: InternalAlignment(g76,g74)
    c: Block(g68)
    c: Block(g74)
    c: Coincident(g77,g68)
    c: Coincident(g77,g74)
    c: Vertical(g77)
    c: Coincident(g78,g68)
    c: Coincident(g78,g50)
    c: Coincident(g79,g50)
    c: Coincident(g79,g74)
    c: Weight(g80) = 1
    c: Equal(g80,g81)
    c: Equal(g80,g82)
    c: InternalAlignment(g80,g83)
    c: InternalAlignment(g81,g83)
    c: InternalAlignment(g82,g83)
    c: InternalAlignment(g84,g83)
    c: InternalAlignment(g85,g83)
    c: Weight(g86) = 1
    c: Equal(g86,g87)
    c: Equal(g86,g88)
    c: InternalAlignment(g86,g89)
    c: InternalAlignment(g87,g89)
    c: InternalAlignment(g88,g89)
    c: InternalAlignment(g90,g89)
    c: InternalAlignment(g91,g89)
    c: Block(g83)
    c: Block(g89)
    c: Coincident(g92,g83)
    c: Coincident(g92,g89)
    c: Vertical(g92)
    c: Coincident(g93,g83)
    c: Coincident(g93,g44)
    c: Coincident(g94,g44)
    c: Coincident(g94,g89)
    c: Weight(g95) = 1
    c: Equal(g95,g96)
    c: Equal(g95,g97)
    c: InternalAlignment(g95,g98)
    c: InternalAlignment(g96,g98)
    c: InternalAlignment(g97,g98)
    c: InternalAlignment(g99,g98)
    c: InternalAlignment(g100,g98)
    c: Weight(g101) = 1
    c: Equal(g101,g102)
    c: Equal(g101,g103)
    c: InternalAlignment(g101,g104)
    c: InternalAlignment(g102,g104)
    c: InternalAlignment(g103,g104)
    c: InternalAlignment(g105,g104)
    c: InternalAlignment(g106,g104)
    c: Block(g98)
    c: Block(g104)
    c: Coincident(g107,g98)
    c: Coincident(g107,g104)
    c: Vertical(g107)
    c: Coincident(g108,g104)
    c: Coincident(g108,g62)
    c: Coincident(g109,g62)
    c: Coincident(g109,g98)
    c: Weight(g110) = 1
    c: Equal(g110,g111)
    c: Equal(g110,g112)
    c: InternalAlignment(g110,g113)
    c: InternalAlignment(g111,g113)
    c: InternalAlignment(g112,g113)
    c: InternalAlignment(g114,g113)
    c: InternalAlignment(g115,g113)
    c: Weight(g116) = 1
    c: Equal(g116,g117)
    c: Equal(g116,g118)
    c: InternalAlignment(g116,g119)
    c: InternalAlignment(g117,g119)
    c: InternalAlignment(g118,g119)
    c: InternalAlignment(g120,g119)
    c: InternalAlignment(g121,g119)
    c: Block(g113)
    c: Block(g119)
    c: Coincident(g122,g113)
    c: Coincident(g122,g119)
    c: Vertical(g122)
    c: Coincident(g123,g119)
    c: Coincident(g123,g56)
    c: Coincident(g124,g56)
    c: Coincident(g124,g113)
    c: Weight(g125) = 1
    c: Equal(g125,g126)
    c: Equal(g125,g127)
    c: InternalAlignment(g125,g128)
    c: InternalAlignment(g126,g128)
    c: InternalAlignment(g127,g128)
    c: InternalAlignment(g129,g128)
    c: InternalAlignment(g130,g128)
    c: Weight(g131) = 1
    c: Equal(g131,g132)
    c: Equal(g131,g133)
    c: InternalAlignment(g131,g134)
    c: InternalAlignment(g132,g134)
    c: InternalAlignment(g133,g134)
    c: InternalAlignment(g135,g134)
    c: InternalAlignment(g136,g134)
    c: Weight(g137) = 1
    c: Equal(g137,g138)
    c: Equal(g137,g139)
    c: InternalAlignment(g137,g140)
    c: InternalAlignment(g138,g140)
    c: InternalAlignment(g139,g140)
    c: InternalAlignment(g141,g140)
    c: InternalAlignment(g142,g140)
    c: Weight(g143) = 1
    c: Equal(g143,g144)
    c: Equal(g143,g145)
    c: InternalAlignment(g143,g146)
    c: InternalAlignment(g144,g146)
    c: InternalAlignment(g145,g146)
    c: InternalAlignment(g147,g146)
    c: InternalAlignment(g148,g146)
    c: Block(g146)
    c: Block(g140)
    c: Block(g134)
    c: Block(g128)
    c: Coincident(g149,g25)
    c: Coincident(g149,g146)
    c: Coincident(g150,g146)
    c: Coincident(g150,g140)
    c: Horizontal(g150)
    c: Coincident(g151,g140)
    c: Coincident(g151,g25)
    c: Vertical(g151)
    c: Coincident(g152,g19)
    c: Coincident(g152,g134)
    c: Vertical(g152)
    c: Coincident(g153,g134)
    c: Coincident(g153,g128)
    c: Horizontal(g153)
    c: Coincident(g154,g128)
    c: Coincident(g154,g19)
    c: Weight(g155) = 1
    c: Equal(g155,g156)
    c: Equal(g155,g157)
    c: InternalAlignment(g155,g158)
    c: InternalAlignment(g156,g158)
    c: InternalAlignment(g157,g158)
    c: InternalAlignment(g159,g158)
    c: InternalAlignment(g160,g158)
    c: Weight(g161) = 1
    c: Equal(g161,g162)
    c: Equal(g161,g163)
    c: InternalAlignment(g161,g164)
    c: InternalAlignment(g162,g164)
    c: InternalAlignment(g163,g164)
    c: InternalAlignment(g165,g164)
    c: InternalAlignment(g166,g164)
    c: Weight(g167) = 1
    c: Equal(g167,g168)
    c: Equal(g167,g169)
    c: InternalAlignment(g167,g170)
    c: InternalAlignment(g168,g170)
    c: InternalAlignment(g169,g170)
    c: InternalAlignment(g171,g170)
    c: InternalAlignment(g172,g170)
    c: Weight(g173) = 1
    c: Equal(g173,g174)
    c: Equal(g173,g175)
    c: InternalAlignment(g173,g176)
    c: InternalAlignment(g174,g176)
    c: InternalAlignment(g175,g176)
    c: InternalAlignment(g177,g176)
    c: InternalAlignment(g178,g176)
    c: Block(g176)
    c: Block(g170)
    c: Block(g164)
    c: Block(g158)
    c: Coincident(g179,g170)
    c: Coincident(g179,g7)
    c: Vertical(g179)
    c: Coincident(g180,g13)
    c: Coincident(g180,g164)
    c: Vertical(g180)
    c: Coincident(g181,g158)
    c: Coincident(g181,g13)
    c: Coincident(g182,g7)
    c: Weight(g183) = 1
    c: Equal(g183,g184)
    c: Equal(g183,g185)
    c: InternalAlignment(g183,g186)
    c: InternalAlignment(g184,g186)
    c: InternalAlignment(g185,g186)
    c: InternalAlignment(g187,g186)
    c: InternalAlignment(g188,g186)
    c: Weight(g189) = 1
    c: Equal(g189,g190)
    c: Equal(g189,g191)
    c: InternalAlignment(g189,g192)
    c: InternalAlignment(g190,g192)
    c: InternalAlignment(g191,g192)
    c: InternalAlignment(g193,g192)
    c: InternalAlignment(g194,g192)
    c: Block(g192)
    c: Block(g186)
    c: Coincident(g195,g192)
    c: Coincident(g195,g31)
    c: Coincident(g196,g31)
    c: Coincident(g196,g186)
    c: Coincident(g197,g186)
    c: Coincident(g197,g192)
    c: Vertical(g197)
    c: Weight(g198) = 1
    c: Equal(g198,g199)
    c: Equal(g198,g200)
    c: InternalAlignment(g198,g201)
    c: InternalAlignment(g199,g201)
    c: InternalAlignment(g200,g201)
    c: InternalAlignment(g202,g201)
    c: InternalAlignment(g203,g201)
    c: Weight(g204) = 1
    c: Equal(g204,g205)
    c: Equal(g204,g206)
    c: InternalAlignment(g204,g207)
    c: InternalAlignment(g205,g207)
    c: InternalAlignment(g206,g207)
    c: InternalAlignment(g208,g207)
    c: InternalAlignment(g209,g207)
    c: Block(g207)
    c: Block(g201)
    c: Coincident(g210,g201)
    c: Coincident(g210,g37)
    c: Coincident(g211,g37)
    c: Coincident(g211,g207)
    c: Coincident(g212,g207)
    c: Coincident(g212,g201)
    c: Vertical(g212)
    c: Horizontal(g213)
    c: Block(g213)
    c: Vertical(g214)
    c: Block(g214)
    c: Block(g215)
    c: Weight(g216) = 1
    c: Equal(g216,g217)
    c: Equal(g216,g218)
    c: InternalAlignment(g216,g219)
    c: InternalAlignment(g217,g219)
    c: InternalAlignment(g218,g219)
    c: InternalAlignment(g220,g219)
    c: InternalAlignment(g221,g219)
    c: Weight(g222) = 1
    c: Equal(g222,g223)
    c: Equal(g222,g224)
    c: InternalAlignment(g222,g225)
    c: InternalAlignment(g223,g225)
    c: InternalAlignment(g224,g225)
    c: InternalAlignment(g226,g225)
    c: InternalAlignment(g227,g225)
    c: Weight(g228) = 1
    c: Equal(g228,g229)
    c: Equal(g228,g230)
    c: InternalAlignment(g228,g231)
    c: InternalAlignment(g229,g231)
    c: InternalAlignment(g230,g231)
    c: InternalAlignment(g232,g231)
    c: InternalAlignment(g233,g231)
    c: Weight(g234) = 1
    c: Equal(g234,g235)
    c: Equal(g234,g236)
    c: InternalAlignment(g234,g237)
    c: InternalAlignment(g235,g237)
    c: InternalAlignment(g236,g237)
    c: InternalAlignment(g238,g237)
    c: InternalAlignment(g239,g237)
    c: Block(g219)
    c: Block(g225)
    c: Block(g231)
    c: Block(g237)
    c: Coincident(g240,g225)
    c: Coincident(g240,g219)
    c: Horizontal(g240)
    c: Block(g182)
    c: Weight(g241) = 1
    c: Equal(g241,g242)
    c: Equal(g241,g243)
    c: InternalAlignment(g241,g244)
    c: InternalAlignment(g242,g244)
    c: InternalAlignment(g243,g244)
    c: InternalAlignment(g245,g244)
    c: InternalAlignment(g246,g244)
    c: Weight(g247) = 1
    c: Equal(g247,g248)
    c: Equal(g247,g249)
    c: InternalAlignment(g247,g250)
    c: InternalAlignment(g248,g250)
    c: InternalAlignment(g249,g250)
    c: InternalAlignment(g251,g250)
    c: InternalAlignment(g252,g250)
    c: Block(g244)
    c: Block(g250)
    c: Coincident(g253,g244)
    c: Coincident(g253,g250)
    c: Weight(g254) = 1
    c: Equal(g254,g255)
    c: Equal(g254,g256)
    c: InternalAlignment(g254,g257)
    c: InternalAlignment(g255,g257)
    c: InternalAlignment(g256,g257)
    c: InternalAlignment(g258,g257)
    c: InternalAlignment(g259,g257)
    c: Weight(g260) = 1
    c: Equal(g260,g261)
    c: Equal(g260,g262)
    c: InternalAlignment(g260,g263)
    c: InternalAlignment(g261,g263)
    c: InternalAlignment(g262,g263)
    c: InternalAlignment(g264,g263)
    c: InternalAlignment(g265,g263)
    c: Weight(g266) = 1
    c: Equal(g266,g267)
    c: Equal(g266,g268)
    c: InternalAlignment(g266,g269)
    c: InternalAlignment(g267,g269)
    c: InternalAlignment(g268,g269)
    c: InternalAlignment(g270,g269)
    c: InternalAlignment(g271,g269)
    c: Block(g269)
    c: Block(g263)
    c: Block(g257)
    c: Coincident(g272,g263)
    c: Coincident(g272,g257)
    c: Coincident(g273,g257)
    c: Coincident(g273,g269)
    c: Vertical(g273)
    c: Coincident(g274,g269)
    c: Coincident(g274,g263)
    c: Horizontal(g274)
    c: Weight(g275) = 1
    c: Equal(g275,g276)
    c: InternalAlignment(g275,g277)
    c: InternalAlignment(g276,g277)
    c: InternalAlignment(g278,g277)
    c: InternalAlignment(g279,g277)
    c: Weight(g280) = 1
    c: InternalAlignment(g281,g283)
    c: InternalAlignment(g282,g283)
    c: InternalAlignment(g284,g283)
    c: InternalAlignment(g285,g283)
    c: Weight(g286) = 1
    c: Equal(g286,g287)
    c: Equal(g286,g288)
    c: InternalAlignment(g286,g289)
    c: InternalAlignment(g287,g289)
    c: InternalAlignment(g288,g289)
    c: InternalAlignment(g290,g289)
    c: InternalAlignment(g291,g289)
    c: Equal(g292,g293)
    c: Equal(g292,g294)
    c: InternalAlignment(g292,g295)
    c: InternalAlignment(g293,g295)
    c: InternalAlignment(g294,g295)
    c: InternalAlignment(g296,g295)
    c: InternalAlignment(g297,g295)
    c: Block(g283)
    c: Block(g289)
    c: Block(g295)
    c: Block(g277)
    c: Coincident(g298,g277)
    c: Coincident(g298,g283)
    c: Horizontal(g298)
    c: Coincident(g299,g283)
    c: Coincident(g299,g289)
    c: Vertical(g299)
    c: Coincident(g300,g289)
    c: Coincident(g300,g295)
    c: Horizontal(g300)
    c: Coincident(g301,g295)
    c: Coincident(g301,g277)
    c: Weight(g302) = 1
    c: Equal(g302,g303)
    c: Equal(g302,g304)
    c: InternalAlignment(g302,g305)
    c: InternalAlignment(g303,g305)
    c: InternalAlignment(g304,g305)
    c: InternalAlignment(g306,g305)
    c: InternalAlignment(g307,g305)
    c: Weight(g308) = 1
    c: Equal(g308,g309)
    c: Equal(g308,g310)
    c: InternalAlignment(g308,g311)
    c: InternalAlignment(g309,g311)
    c: InternalAlignment(g310,g311)
    c: InternalAlignment(g312,g311)
    c: Weight(g314) = 1
    c: Equal(g314,g315)
    c: Equal(g314,g316)
    c: InternalAlignment(g314,g317)
    c: InternalAlignment(g315,g317)
    c: InternalAlignment(g316,g317)
    c: InternalAlignment(g318,g317)
    c: InternalAlignment(g319,g317)
    c: Block(g317)
    c: Block(g311)
    c: Block(g305)
    c: Coincident(g320,g317)
    c: Coincident(g320,g311)
    c: Horizontal(g320)
    c: Coincident(g321,g311)
    c: Coincident(g321,g305)
    c: Vertical(g321)
    c: Coincident(g322,g305)
    c: Coincident(g322,g317)
    c: InternalAlignment(g323,g324)
    c: InternalAlignment(g325,g324)
    c: InternalAlignment(g326,g324)
    c: Block(g324)
    c: Equal(g327,g328)
    c: Equal(g327,g329)
    c: InternalAlignment(g327,g330)
    c: InternalAlignment(g328,g330)
    c: InternalAlignment(g329,g330)
    c: InternalAlignment(g331,g330)
    c: InternalAlignment(g332,g330)
    c: Block(g330)
    c: Coincident(g333,g324)
    c: Horizontal(g333)
    c: Block(g333)
    c: Coincident(g334,g324)
    c: Coincident(g334,g250)
    c: Vertical(g334)
    c: Coincident(g335,g330)
    c: Coincident(g335,g244)
    c: Vertical(g335)
    c: Block(g336)
    c: Block(g2)
    c: Distance(g334) = 119.89
    c: Coincident(g337,g336)
    c: Coincident(g337,g2)
    c: Coincident(g338,g2)
    c: Coincident(g338,g336)
    c: Block(g3)
    c: Block(g339)
    c: Coincident(g340,g339)
    c: Coincident(g340,g3)
    c: Coincident(g341,g339)
    c: Coincident(g341,g3)
    c: Block(g341)
    c: Block(g340)
    c: Weight(g342) = 1
    c: Equal(g342,g343)
    c: Equal(g342,g344)
    c: InternalAlignment(g342,g345)
    c: InternalAlignment(g343,g345)
    c: InternalAlignment(g344,g345)
    c: InternalAlignment(g346,g345)
    c: InternalAlignment(g347,g345)
    c: Weight(g348) = 1
    c: Equal(g348,g349)
    c: Equal(g348,g350)
    c: InternalAlignment(g348,g351)
    c: InternalAlignment(g349,g351)
    c: InternalAlignment(g350,g351)
    c: InternalAlignment(g352,g351)
    c: InternalAlignment(g353,g351)
    c: Weight(g354) = 1
    c: Equal(g354,g355)
    c: Equal(g354,g356)
    c: InternalAlignment(g354,g357)
    c: InternalAlignment(g355,g357)
    c: InternalAlignment(g356,g357)
    c: InternalAlignment(g358,g357)
    c: InternalAlignment(g359,g357)
    c: Weight(g360) = 1
    c: Equal(g360,g361)
    c: Equal(g360,g362)
    c: InternalAlignment(g360,g363)
    c: InternalAlignment(g361,g363)
    c: InternalAlignment(g362,g363)
    c: InternalAlignment(g364,g363)
    c: InternalAlignment(g365,g363)
    c: Block(g363)
    c: Block(g357)
    c: Block(g351)
    c: Block(g345)
    c: Coincident(g366,g363)
    c: Coincident(g366,g345)
    c: Vertical(g366)
    c: Coincident(g367,g345)
    c: Coincident(g367,g351)
    c: Coincident(g368,g351)
    c: Coincident(g368,g357)
    c: Vertical(g368)
    c: Coincident(g369,g357)
    c: Coincident(g369,g363)
    c: Horizontal(g369)
    c: Vertical(g370)
    c: Coincident(g371,g0)
    c: Coincident(g371,g1)
    c: Horizontal(g371)
    c: Block(g371)
    c: Distance(g371) = 450
    c: Block(g370)
    c: Distance(g0) = 240
    c: Horizontal(g372)
    c: Distance(g372) = 12
    c: Vertical(g373)
    c: Distance(g373) = 12
    c: Coincident(g374,g372)
    c: Vertical(g374)
    c: Horizontal(g375)
    c: Vertical(g376)
    c: Distance(g376) = 6
    c: Coincident(g376,g372)
    c: Coincident(g375,g372)
    c: Block(g374)
    c: Coincident(g377,g374)
    c: Horizontal(g377)
    c: Distance(g377) = 6
    c: Vertical(g378)
    c: Distance(g378) = 3
    c: Vertical(g379)
    c: Distance(g379) = 3
    c: Coincident(g373,g378)
    c: Coincident(g385,g379)
    c: Weight(g380) = 1
    c: Equal(g380,g381)
    c: Coincident(g381,g375)
    c: Equal(g380,g382)
    c: Coincident(g382,g376)
    c: Equal(g380,g383)
    c: Coincident(g383,g377)
    c: Equal(g380,g384)
    c: Coincident(g385,g378)
    c: InternalAlignment(g380-g384 -> g385) x5
    c: InternalAlignment(g386,g385)
    c: InternalAlignment(g387,g385)
    c: InternalAlignment(g388,g385)
    c: Coincident(g389,g164)
    c: Coincident(g389,g158)
    c: Horizontal(g389)
    c: Block(g385)
    c: Vertical(g390)
    c: Distance(g390) = 12
    c: Horizontal(g391)
    c: Distance(g391) = 12
    c: Coincident(g392,g391)
    c: Vertical(g392)
    c: Distance(g392) = 12
    c: Horizontal(g393)
    c: Distance(g393) = 6
    c: Coincident(g393,g391)
    c: Vertical(g394)
    c: Distance(g394) = 6
    c: Coincident(g394,g391)
    c: Vertical(g395)
    c: Distance(g395) = 3
    c: Vertical(g396)
    c: Distance(g396) = 6
    c: Coincident(g396,g395)
    c: Coincident(g402,g395)
    c: Weight(g397) = 1
    c: Equal(g397,g398)
    c: Coincident(g398,g393)
    c: Equal(g397,g399)
    c: Coincident(g399,g394)
    c: Equal(g397,g400)
    c: Equal(g397,g401)
    c: Coincident(g402,g396)
    c: InternalAlignment(g397-g401 -> g402) x5
    c: InternalAlignment(g403,g402)
    c: InternalAlignment(g404,g402)
    c: InternalAlignment(g405,g402)
    c: Coincident(g406,g390)
    c: Coincident(g406,g170)
    c: Horizontal(g406)
    c: Block(g402)
    c: Coincident(g407,g176)
    c: Coincident(g407,g390)
    c: Horizontal(g407)
    c: Block(g406)
    c: Coincident(g409,g390)
    c: PointOnObject(g409,g153)
    c: Vertical(g409)
    c: Block(g410)
    c: Coincident(g411,g410)
    c: Vertical(g411)
    c: PointOnObject(g411,g40)
    c: Block(g411)
    c: Coincident(g412,g410)
    c: Vertical(g412)
    c: Block(g412)
    c: Vertical(g413)
    c: Distance(g413) = 3
    c: Equal(g380,g416) = 1
    c: Equal(g416,g417)
    c: InternalAlignment(g416,g418)
    c: InternalAlignment(g417,g418)
    c: InternalAlignment(g414,g418)
    c: InternalAlignment(g415,g418)
    c: InternalAlignment(g419,g418)
    c: Block(g418)
    c: Coincident(g419,g413)
    c: Coincident(g420,g418)
    c: PointOnObject(g420,g150)
    c: Vertical(g420)
    c: PointOnObject(g421,g211)
    c: Block(g421)
    c: Distance(g422) = 3
    c: Block(g422)
FEATURE [Part::Extrusion] Extrude005
  Base = -> Sketch003
  Dir = (0,0,1)
  DirMode = 2
  FaceMakerClass = Part::FaceMakerBullseye
  LengthFwd = 24
  LengthRev = 0
  Solid = true
  Symmetric = false
